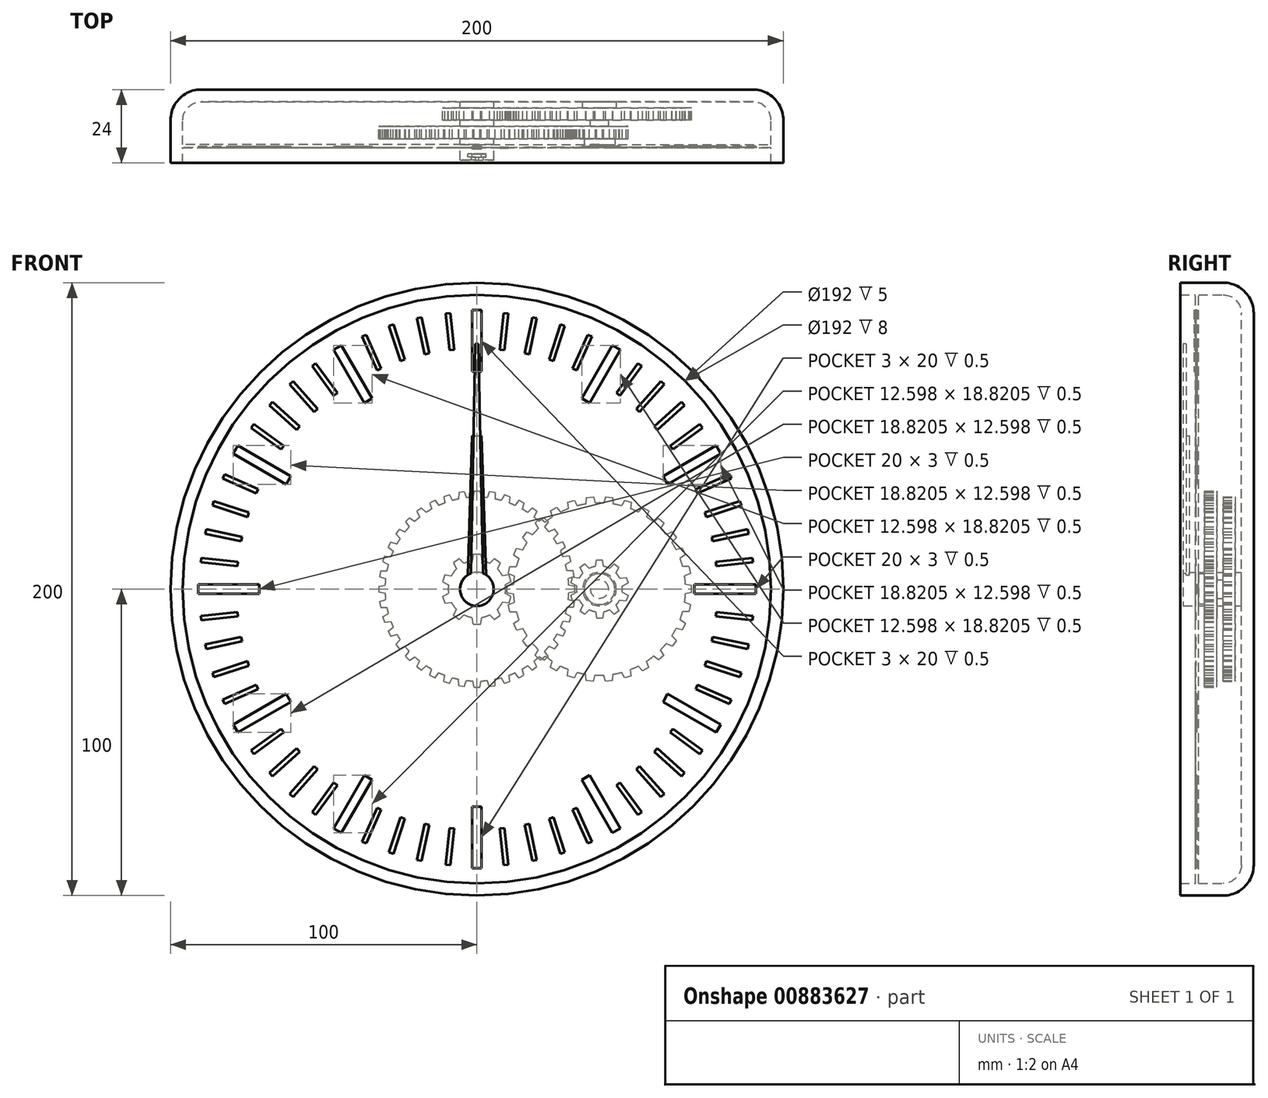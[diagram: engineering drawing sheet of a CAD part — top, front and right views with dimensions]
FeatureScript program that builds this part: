
annotation { "Feature Type Name" : "Feature", "Feature Type Description" : "" }
export const myFeature = defineFeature(function(context is Context, id is Id, definition is map)
    precondition{}
    {
        {
            var Q0;
            Q0=qCreatedBy(makeId("Front.planeOp"),FACE);
            var sketch = newSketch(context, id + "F0", { "sketchPlane" : qUnion([Q0])});
            skCircle(sketch, "E0", {"center": v(0, 0) * mm, "radius": 100 * mm});
            skSolve(sketch);
        }
        {
            var Q0;
            Q0 = qSketchRegion(id + "F0", true);
            extrude(context, id + "F1", {"entities" : qUnion([Q0]), "depth" : 24 * mm, "offsetDistance" : 25 * mm});
        }
        {
            var Q0;
            Q0=makeQuery(id+"F1.opExtrude","CAP_EDGE",EDGE,{"disambiguationData":[OSD([sQuery(id+"F0.wireOp",EDGE,"E0")])],"isStart":true});
            fillet(context, id + "F2", {"entities" : qUnion([Q0]), "radius" : 10 * mm, "tangentPropagation" : true, "allowEdgeOverflow" : false});
        }
        {
            var Q0;
            Q0=makeQuery(id+"F1.opExtrude","CAP_FACE",FACE,{"disambiguationData":[OSD([sQuery(id+"F0.wireOp",EDGE,"E0")])],"isStart":false});
            shell(context, id + "F3", {"entities" : qUnion([Q0]), "thickness" : 4 * mm});
        }
        {
            var Q0;
            {var subQ0=sQuery(id+"F0.wireOp",EDGE,"E0");Q0=makeQuery(id+"F3.opShell","OFFSET_FACE",FACE,{"disambiguationData":[OSD([subQ0]),TDD([makeQuery(id+"F1.opExtrude","CAP_FACE",FACE,{"disambiguationData":[OSD([subQ0])],"isStart":true})])]});}
            var sketch = newSketch(context, id + "F4", { "sketchPlane" : qUnion([Q0])});
            skCircle(sketch, "E1", {"center": v(0, 0) * mm, "radius": 3 * mm});
            skCircle(sketch, "E2", {"center": v(0, 0) * mm, "radius": 5.5 * mm});
            skCircle(sketch, "E3", {"center": v(40, 0) * mm, "radius": 3 * mm});
            skCircle(sketch, "E4", {"center": v(40, 0) * mm, "radius": 5.5 * mm});
            skSolve(sketch);
        }
        {
            var Q0;
            Q0 = qSketchRegion(id + "F4", true);
            extrude(context, id + "F5", {"entities" : qUnion([Q0]), "operationType" : NewBodyOperationType.ADD, "depth" : 2 * mm, "offsetDistance" : 25 * mm});
        }
        {
            var Q0;
            {var subQ0=sQuery(id+"F0.wireOp",EDGE,"E0");Q0=makeQuery(id+"F5.boolean.opBoolean","SPLIT",FACE,{"disambiguationData":[TD([makeQuery(id+"F5.opExtrude","SWEPT_FACE",FACE,{"disambiguationData":[OSD([sQuery(id+"F4.wireOp",EDGE,"E1")])]})])],"derivedFrom":makeQuery(id+"F3.opShell","OFFSET_FACE",FACE,{"disambiguationData":[OSD([subQ0]),TDD([makeQuery(id+"F1.opExtrude","CAP_FACE",FACE,{"disambiguationData":[OSD([subQ0])],"isStart":true})])]})});}
            extrude(context, id + "F6", {"entities" : qUnion([Q0]), "depth" : 19 * mm, "offsetDistance" : 25 * mm});
        }
        {
            var Q0;
            {var subQ0=sQuery(id+"F0.wireOp",EDGE,"E0");Q0=makeQuery(id+"F5.boolean.opBoolean","SPLIT",FACE,{"disambiguationData":[TD([makeQuery(id+"F5.opExtrude","SWEPT_FACE",FACE,{"disambiguationData":[OSD([sQuery(id+"F4.wireOp",EDGE,"E3")])]})])],"derivedFrom":makeQuery(id+"F3.opShell","OFFSET_FACE",FACE,{"disambiguationData":[OSD([subQ0]),TDD([makeQuery(id+"F1.opExtrude","CAP_FACE",FACE,{"disambiguationData":[OSD([subQ0])],"isStart":true})])]})});}
            extrude(context, id + "F7", {"entities" : qUnion([Q0]), "depth" : 8 * mm, "offsetDistance" : 25 * mm});
        }
        {
            var Q0;
            Q0=makeQuery(id+"F5.opExtrude","CAP_FACE",FACE,{"disambiguationData":[OSD([sQuery(id+"F4.wireOp",EDGE,"E1"),sQuery(id+"F4.wireOp",EDGE,"E2")])],"isStart":false});
            var sketch = newSketch(context, id + "F8", { "sketchPlane" : qUnion([Q0])});
            skCircle(sketch, "E5", {"center": v(0, 0) * mm, "radius": 9.38 * mm});
            skLineSegment(sketch, "E6", {"start": v(0, 11.38) * mm, "end": v(1.18, 11.38) * mm});
            skLineSegment(sketch, "E7", {"start": v(1.18, 11.38) * mm, "end": v(1.55, 9.25) * mm});
            skLineSegment(sketch, "E8.MirrorCS", {"start": v(0, 11.38) * mm, "end": v(-1.18, 11.38) * mm});
            skLineSegment(sketch, "E9.MirrorCS", {"start": v(-1.18, 11.38) * mm, "end": v(-1.55, 9.25) * mm});
            skLineSegment(sketch, "E10.1.0", {"start": v(-7.64, 8.51) * mm, "end": v(-6.7, 6.57) * mm});
            skLineSegment(sketch, "E10.1.1", {"start": v(-6.69, 9.2) * mm, "end": v(-7.64, 8.51) * mm});
            skLineSegment(sketch, "E10.1.2", {"start": v(-6.69, 9.2) * mm, "end": v(-5.73, 9.9) * mm});
            skLineSegment(sketch, "E10.1.3", {"start": v(-5.73, 9.9) * mm, "end": v(-4.18, 8.4) * mm});
            skLineSegment(sketch, "E10.2.0", {"start": v(-11.18, 2.4) * mm, "end": v(-9.27, 1.38) * mm});
            skLineSegment(sketch, "E10.2.1", {"start": v(-10.82, 3.52) * mm, "end": v(-11.18, 2.4) * mm});
            skLineSegment(sketch, "E10.2.2", {"start": v(-10.82, 3.52) * mm, "end": v(-10.45, 4.64) * mm});
            skLineSegment(sketch, "E10.2.3", {"start": v(-10.45, 4.64) * mm, "end": v(-8.31, 4.33) * mm});
            skLineSegment(sketch, "E11.2.3.0", {"start": v(-10.45, -4.64) * mm, "end": v(-8.31, -4.33) * mm});
            skLineSegment(sketch, "E11.3.3.0", {"start": v(-10.82, -3.52) * mm, "end": v(-10.45, -4.64) * mm});
            skLineSegment(sketch, "E11.6.3.0", {"start": v(-10.82, -3.52) * mm, "end": v(-11.18, -2.4) * mm});
            skLineSegment(sketch, "E11.9.3.0", {"start": v(-11.18, -2.4) * mm, "end": v(-9.27, -1.38) * mm});
            skLineSegment(sketch, "E11.2.4.0", {"start": v(-5.73, -9.9) * mm, "end": v(-4.18, -8.4) * mm});
            skLineSegment(sketch, "E11.3.4.0", {"start": v(-6.69, -9.2) * mm, "end": v(-5.73, -9.9) * mm});
            skLineSegment(sketch, "E11.6.4.0", {"start": v(-6.69, -9.2) * mm, "end": v(-7.64, -8.51) * mm});
            skLineSegment(sketch, "E11.9.4.0", {"start": v(-7.64, -8.51) * mm, "end": v(-6.7, -6.57) * mm});
            skLineSegment(sketch, "E11.2.5.0", {"start": v(1.18, -11.38) * mm, "end": v(1.55, -9.25) * mm});
            skLineSegment(sketch, "E11.3.5.0", {"start": v(0, -11.38) * mm, "end": v(1.18, -11.38) * mm});
            skLineSegment(sketch, "E11.6.5.0", {"start": v(0, -11.38) * mm, "end": v(-1.18, -11.38) * mm});
            skLineSegment(sketch, "E11.9.5.0", {"start": v(-1.18, -11.38) * mm, "end": v(-1.55, -9.25) * mm});
            skLineSegment(sketch, "E11.2.6.0", {"start": v(7.64, -8.51) * mm, "end": v(6.7, -6.57) * mm});
            skLineSegment(sketch, "E11.3.6.0", {"start": v(6.69, -9.2) * mm, "end": v(7.64, -8.51) * mm});
            skLineSegment(sketch, "E11.6.6.0", {"start": v(6.69, -9.2) * mm, "end": v(5.73, -9.9) * mm});
            skLineSegment(sketch, "E11.9.6.0", {"start": v(5.73, -9.9) * mm, "end": v(4.18, -8.4) * mm});
            skLineSegment(sketch, "E11.2.7.0", {"start": v(11.18, -2.4) * mm, "end": v(9.27, -1.38) * mm});
            skLineSegment(sketch, "E11.3.7.0", {"start": v(10.82, -3.52) * mm, "end": v(11.18, -2.4) * mm});
            skLineSegment(sketch, "E11.6.7.0", {"start": v(10.82, -3.52) * mm, "end": v(10.45, -4.64) * mm});
            skLineSegment(sketch, "E11.9.7.0", {"start": v(10.45, -4.64) * mm, "end": v(8.31, -4.33) * mm});
            skLineSegment(sketch, "E11.2.8.0", {"start": v(10.45, 4.64) * mm, "end": v(8.31, 4.33) * mm});
            skLineSegment(sketch, "E11.3.8.0", {"start": v(10.82, 3.52) * mm, "end": v(10.45, 4.64) * mm});
            skLineSegment(sketch, "E11.6.8.0", {"start": v(10.82, 3.52) * mm, "end": v(11.18, 2.4) * mm});
            skLineSegment(sketch, "E11.9.8.0", {"start": v(11.18, 2.4) * mm, "end": v(9.27, 1.38) * mm});
            skLineSegment(sketch, "E11.2.9.0", {"start": v(5.73, 9.9) * mm, "end": v(4.18, 8.4) * mm});
            skLineSegment(sketch, "E11.3.9.0", {"start": v(6.69, 9.2) * mm, "end": v(5.73, 9.9) * mm});
            skLineSegment(sketch, "E11.6.9.0", {"start": v(6.69, 9.2) * mm, "end": v(7.64, 8.51) * mm});
            skLineSegment(sketch, "E11.9.9.0", {"start": v(7.64, 8.51) * mm, "end": v(6.7, 6.57) * mm});
            skSolve(sketch);
        }
        {
            var Q0;
            Q0 = qSketchRegion(id + "F8", true);
            extrude(context, id + "F9", {"entities" : qUnion([Q0]), "operationType" : NewBodyOperationType.ADD, "depth" : 4 * mm, "offsetDistance" : 25 * mm});
        }
        {
            var Q0;
            Q0=makeQuery(id+"F5.opExtrude","CAP_FACE",FACE,{"disambiguationData":[OSD([sQuery(id+"F4.wireOp",EDGE,"E3"),sQuery(id+"F4.wireOp",EDGE,"E4")])],"isStart":false});
            var sketch = newSketch(context, id + "F10", { "sketchPlane" : qUnion([Q0])});
            skCircle(sketch, "E12", {"center": v(40, 0) * mm, "radius": 28.12 * mm});
            skLineSegment(sketch, "E13", {"start": v(9.88, 0) * mm, "end": v(9.88, 1.18) * mm});
            skLineSegment(sketch, "E14", {"start": v(9.88, 1.18) * mm, "end": v(11.92, 1.54) * mm});
            skLineSegment(sketch, "E15.MirrorCS", {"start": v(9.88, 0) * mm, "end": v(9.88, -1.18) * mm});
            skLineSegment(sketch, "E16.MirrorCS", {"start": v(9.88, -1.18) * mm, "end": v(11.92, -1.54) * mm});
            skLineSegment(sketch, "E17.1.0", {"start": v(10.29, -5.11) * mm, "end": v(12.21, -4.33) * mm});
            skLineSegment(sketch, "E17.1.1", {"start": v(10.53, -6.26) * mm, "end": v(10.29, -5.11) * mm});
            skLineSegment(sketch, "E17.1.2", {"start": v(10.53, -6.26) * mm, "end": v(10.78, -7.42) * mm});
            skLineSegment(sketch, "E17.1.3", {"start": v(10.78, -7.42) * mm, "end": v(12.85, -7.34) * mm});
            skLineSegment(sketch, "E17.2.0", {"start": v(12, -11.18) * mm, "end": v(13.72, -10.02) * mm});
            skLineSegment(sketch, "E17.2.1", {"start": v(12.48, -12.25) * mm, "end": v(12, -11.18) * mm});
            skLineSegment(sketch, "E17.2.2", {"start": v(12.48, -12.25) * mm, "end": v(12.96, -13.33) * mm});
            skLineSegment(sketch, "E17.2.3", {"start": v(12.96, -13.33) * mm, "end": v(14.97, -12.83) * mm});
            skLineSegment(sketch, "E18.1.3.0", {"start": v(14.94, -16.75) * mm, "end": v(16.38, -15.26) * mm});
            skLineSegment(sketch, "E18.3.3.0", {"start": v(15.63, -17.7) * mm, "end": v(14.94, -16.75) * mm});
            skLineSegment(sketch, "E18.6.3.0", {"start": v(15.63, -17.7) * mm, "end": v(16.32, -18.66) * mm});
            skLineSegment(sketch, "E18.9.3.0", {"start": v(16.32, -18.66) * mm, "end": v(18.18, -17.75) * mm});
            skLineSegment(sketch, "E18.1.4.0", {"start": v(18.97, -21.6) * mm, "end": v(20.07, -19.84) * mm});
            skLineSegment(sketch, "E18.3.4.0", {"start": v(19.84, -22.39) * mm, "end": v(18.97, -21.6) * mm});
            skLineSegment(sketch, "E18.6.4.0", {"start": v(19.84, -22.39) * mm, "end": v(20.72, -23.18) * mm});
            skLineSegment(sketch, "E18.9.4.0", {"start": v(20.72, -23.18) * mm, "end": v(22.35, -21.9) * mm});
            skLineSegment(sketch, "E18.1.5.0", {"start": v(23.92, -25.5) * mm, "end": v(24.63, -23.55) * mm});
            skLineSegment(sketch, "E18.3.5.0", {"start": v(24.94, -26.09) * mm, "end": v(23.92, -25.5) * mm});
            skLineSegment(sketch, "E18.6.5.0", {"start": v(24.94, -26.09) * mm, "end": v(25.96, -26.68) * mm});
            skLineSegment(sketch, "E18.9.5.0", {"start": v(25.96, -26.68) * mm, "end": v(27.3, -25.09) * mm});
            skLineSegment(sketch, "E18.1.6.0", {"start": v(29.57, -28.29) * mm, "end": v(29.86, -26.23) * mm});
            skLineSegment(sketch, "E18.3.6.0", {"start": v(30.7, -28.65) * mm, "end": v(29.57, -28.29) * mm});
            skLineSegment(sketch, "E18.6.6.0", {"start": v(30.7, -28.65) * mm, "end": v(31.81, -29.01) * mm});
            skLineSegment(sketch, "E18.9.6.0", {"start": v(31.81, -29.01) * mm, "end": v(32.78, -27.18) * mm});
            skLineSegment(sketch, "E18.1.7.0", {"start": v(35.68, -29.84) * mm, "end": v(35.53, -27.77) * mm});
            skLineSegment(sketch, "E18.3.7.0", {"start": v(36.85, -29.96) * mm, "end": v(35.68, -29.84) * mm});
            skLineSegment(sketch, "E18.6.7.0", {"start": v(36.85, -29.96) * mm, "end": v(38.02, -30.08) * mm});
            skLineSegment(sketch, "E18.9.7.0", {"start": v(38.02, -30.08) * mm, "end": v(38.6, -28.09) * mm});
            skLineSegment(sketch, "E18.1.8.0", {"start": v(41.98, -30.08) * mm, "end": v(41.4, -28.09) * mm});
            skLineSegment(sketch, "E18.3.8.0", {"start": v(43.15, -29.96) * mm, "end": v(41.98, -30.08) * mm});
            skLineSegment(sketch, "E18.6.8.0", {"start": v(43.15, -29.96) * mm, "end": v(44.32, -29.84) * mm});
            skLineSegment(sketch, "E18.9.8.0", {"start": v(44.32, -29.84) * mm, "end": v(44.47, -27.77) * mm});
            skLineSegment(sketch, "E18.1.9.0", {"start": v(48.19, -29.01) * mm, "end": v(47.22, -27.18) * mm});
            skLineSegment(sketch, "E18.3.9.0", {"start": v(49.3, -28.65) * mm, "end": v(48.19, -29.01) * mm});
            skLineSegment(sketch, "E18.6.9.0", {"start": v(49.3, -28.65) * mm, "end": v(50.43, -28.29) * mm});
            skLineSegment(sketch, "E18.9.9.0", {"start": v(50.43, -28.29) * mm, "end": v(50.14, -26.23) * mm});
            skLineSegment(sketch, "E18.1.10.0", {"start": v(54.04, -26.68) * mm, "end": v(52.7, -25.09) * mm});
            skLineSegment(sketch, "E18.3.10.0", {"start": v(55.06, -26.09) * mm, "end": v(54.04, -26.68) * mm});
            skLineSegment(sketch, "E18.6.10.0", {"start": v(55.06, -26.09) * mm, "end": v(56.08, -25.5) * mm});
            skLineSegment(sketch, "E18.9.10.0", {"start": v(56.08, -25.5) * mm, "end": v(55.37, -23.55) * mm});
            skLineSegment(sketch, "E18.1.11.0", {"start": v(59.28, -23.18) * mm, "end": v(57.65, -21.9) * mm});
            skLineSegment(sketch, "E18.3.11.0", {"start": v(60.16, -22.39) * mm, "end": v(59.28, -23.18) * mm});
            skLineSegment(sketch, "E18.6.11.0", {"start": v(60.16, -22.39) * mm, "end": v(61.03, -21.6) * mm});
            skLineSegment(sketch, "E18.9.11.0", {"start": v(61.03, -21.6) * mm, "end": v(59.93, -19.84) * mm});
            skLineSegment(sketch, "E18.1.12.0", {"start": v(63.68, -18.66) * mm, "end": v(61.82, -17.75) * mm});
            skLineSegment(sketch, "E18.3.12.0", {"start": v(64.37, -17.7) * mm, "end": v(63.68, -18.66) * mm});
            skLineSegment(sketch, "E18.6.12.0", {"start": v(64.37, -17.7) * mm, "end": v(65.06, -16.75) * mm});
            skLineSegment(sketch, "E18.9.12.0", {"start": v(65.06, -16.75) * mm, "end": v(63.62, -15.26) * mm});
            skLineSegment(sketch, "E18.1.13.0", {"start": v(67.04, -13.33) * mm, "end": v(65.03, -12.83) * mm});
            skLineSegment(sketch, "E18.3.13.0", {"start": v(67.52, -12.25) * mm, "end": v(67.04, -13.33) * mm});
            skLineSegment(sketch, "E18.6.13.0", {"start": v(67.52, -12.25) * mm, "end": v(68, -11.18) * mm});
            skLineSegment(sketch, "E18.9.13.0", {"start": v(68, -11.18) * mm, "end": v(66.28, -10.02) * mm});
            skLineSegment(sketch, "E18.1.14.0", {"start": v(69.22, -7.42) * mm, "end": v(67.15, -7.34) * mm});
            skLineSegment(sketch, "E18.3.14.0", {"start": v(69.47, -6.26) * mm, "end": v(69.22, -7.42) * mm});
            skLineSegment(sketch, "E18.6.14.0", {"start": v(69.47, -6.26) * mm, "end": v(69.71, -5.11) * mm});
            skLineSegment(sketch, "E18.9.14.0", {"start": v(69.71, -5.11) * mm, "end": v(67.79, -4.33) * mm});
            skLineSegment(sketch, "E18.1.15.0", {"start": v(70.13, -1.18) * mm, "end": v(68.08, -1.54) * mm});
            skLineSegment(sketch, "E18.3.15.0", {"start": v(70.12, 0) * mm, "end": v(70.12, -1.18) * mm});
            skLineSegment(sketch, "E18.6.15.0", {"start": v(70.12, 0) * mm, "end": v(70.12, 1.18) * mm});
            skLineSegment(sketch, "E18.9.15.0", {"start": v(70.13, 1.18) * mm, "end": v(68.08, 1.54) * mm});
            skLineSegment(sketch, "E18.1.16.0", {"start": v(69.71, 5.11) * mm, "end": v(67.79, 4.33) * mm});
            skLineSegment(sketch, "E18.3.16.0", {"start": v(69.47, 6.26) * mm, "end": v(69.71, 5.11) * mm});
            skLineSegment(sketch, "E18.6.16.0", {"start": v(69.47, 6.26) * mm, "end": v(69.22, 7.42) * mm});
            skLineSegment(sketch, "E18.9.16.0", {"start": v(69.22, 7.42) * mm, "end": v(67.15, 7.34) * mm});
            skLineSegment(sketch, "E18.1.17.0", {"start": v(68, 11.18) * mm, "end": v(66.28, 10.02) * mm});
            skLineSegment(sketch, "E18.3.17.0", {"start": v(67.52, 12.25) * mm, "end": v(68, 11.18) * mm});
            skLineSegment(sketch, "E18.6.17.0", {"start": v(67.52, 12.25) * mm, "end": v(67.04, 13.33) * mm});
            skLineSegment(sketch, "E18.9.17.0", {"start": v(67.04, 13.33) * mm, "end": v(65.03, 12.83) * mm});
            skLineSegment(sketch, "E18.1.18.0", {"start": v(65.06, 16.75) * mm, "end": v(63.62, 15.26) * mm});
            skLineSegment(sketch, "E18.3.18.0", {"start": v(64.37, 17.7) * mm, "end": v(65.06, 16.75) * mm});
            skLineSegment(sketch, "E18.6.18.0", {"start": v(64.37, 17.7) * mm, "end": v(63.68, 18.66) * mm});
            skLineSegment(sketch, "E18.9.18.0", {"start": v(63.68, 18.66) * mm, "end": v(61.82, 17.75) * mm});
            skLineSegment(sketch, "E18.1.19.0", {"start": v(61.03, 21.6) * mm, "end": v(59.93, 19.84) * mm});
            skLineSegment(sketch, "E18.3.19.0", {"start": v(60.16, 22.39) * mm, "end": v(61.03, 21.6) * mm});
            skLineSegment(sketch, "E18.6.19.0", {"start": v(60.16, 22.39) * mm, "end": v(59.28, 23.18) * mm});
            skLineSegment(sketch, "E18.9.19.0", {"start": v(59.28, 23.18) * mm, "end": v(57.65, 21.9) * mm});
            skLineSegment(sketch, "E18.1.20.0", {"start": v(56.08, 25.5) * mm, "end": v(55.37, 23.55) * mm});
            skLineSegment(sketch, "E18.3.20.0", {"start": v(55.06, 26.09) * mm, "end": v(56.08, 25.5) * mm});
            skLineSegment(sketch, "E18.6.20.0", {"start": v(55.06, 26.09) * mm, "end": v(54.04, 26.68) * mm});
            skLineSegment(sketch, "E18.9.20.0", {"start": v(54.04, 26.68) * mm, "end": v(52.7, 25.09) * mm});
            skLineSegment(sketch, "E18.1.21.0", {"start": v(50.43, 28.29) * mm, "end": v(50.14, 26.23) * mm});
            skLineSegment(sketch, "E18.3.21.0", {"start": v(49.3, 28.65) * mm, "end": v(50.43, 28.29) * mm});
            skLineSegment(sketch, "E18.6.21.0", {"start": v(49.3, 28.65) * mm, "end": v(48.19, 29.01) * mm});
            skLineSegment(sketch, "E18.9.21.0", {"start": v(48.19, 29.01) * mm, "end": v(47.22, 27.18) * mm});
            skLineSegment(sketch, "E18.1.22.0", {"start": v(44.32, 29.84) * mm, "end": v(44.47, 27.77) * mm});
            skLineSegment(sketch, "E18.3.22.0", {"start": v(43.15, 29.96) * mm, "end": v(44.32, 29.84) * mm});
            skLineSegment(sketch, "E18.6.22.0", {"start": v(43.15, 29.96) * mm, "end": v(41.98, 30.08) * mm});
            skLineSegment(sketch, "E18.9.22.0", {"start": v(41.98, 30.08) * mm, "end": v(41.4, 28.09) * mm});
            skLineSegment(sketch, "E18.1.23.0", {"start": v(38.02, 30.08) * mm, "end": v(38.6, 28.09) * mm});
            skLineSegment(sketch, "E18.3.23.0", {"start": v(36.85, 29.96) * mm, "end": v(38.02, 30.08) * mm});
            skLineSegment(sketch, "E18.6.23.0", {"start": v(36.85, 29.96) * mm, "end": v(35.68, 29.84) * mm});
            skLineSegment(sketch, "E18.9.23.0", {"start": v(35.68, 29.84) * mm, "end": v(35.53, 27.77) * mm});
            skLineSegment(sketch, "E18.1.24.0", {"start": v(31.81, 29.01) * mm, "end": v(32.78, 27.18) * mm});
            skLineSegment(sketch, "E18.3.24.0", {"start": v(30.7, 28.65) * mm, "end": v(31.81, 29.01) * mm});
            skLineSegment(sketch, "E18.6.24.0", {"start": v(30.7, 28.65) * mm, "end": v(29.57, 28.29) * mm});
            skLineSegment(sketch, "E18.9.24.0", {"start": v(29.57, 28.29) * mm, "end": v(29.86, 26.23) * mm});
            skLineSegment(sketch, "E18.1.25.0", {"start": v(25.96, 26.68) * mm, "end": v(27.3, 25.09) * mm});
            skLineSegment(sketch, "E18.3.25.0", {"start": v(24.94, 26.09) * mm, "end": v(25.96, 26.68) * mm});
            skLineSegment(sketch, "E18.6.25.0", {"start": v(24.94, 26.09) * mm, "end": v(23.92, 25.5) * mm});
            skLineSegment(sketch, "E18.9.25.0", {"start": v(23.92, 25.5) * mm, "end": v(24.63, 23.55) * mm});
            skLineSegment(sketch, "E18.1.26.0", {"start": v(20.72, 23.18) * mm, "end": v(22.35, 21.9) * mm});
            skLineSegment(sketch, "E18.3.26.0", {"start": v(19.84, 22.39) * mm, "end": v(20.72, 23.18) * mm});
            skLineSegment(sketch, "E18.6.26.0", {"start": v(19.84, 22.39) * mm, "end": v(18.97, 21.6) * mm});
            skLineSegment(sketch, "E18.9.26.0", {"start": v(18.97, 21.6) * mm, "end": v(20.07, 19.84) * mm});
            skLineSegment(sketch, "E18.1.27.0", {"start": v(16.32, 18.66) * mm, "end": v(18.18, 17.75) * mm});
            skLineSegment(sketch, "E18.3.27.0", {"start": v(15.63, 17.7) * mm, "end": v(16.32, 18.66) * mm});
            skLineSegment(sketch, "E18.6.27.0", {"start": v(15.63, 17.7) * mm, "end": v(14.94, 16.75) * mm});
            skLineSegment(sketch, "E18.9.27.0", {"start": v(14.94, 16.75) * mm, "end": v(16.38, 15.26) * mm});
            skLineSegment(sketch, "E18.1.28.0", {"start": v(12.96, 13.33) * mm, "end": v(14.97, 12.83) * mm});
            skLineSegment(sketch, "E18.3.28.0", {"start": v(12.48, 12.25) * mm, "end": v(12.96, 13.33) * mm});
            skLineSegment(sketch, "E18.6.28.0", {"start": v(12.48, 12.25) * mm, "end": v(12, 11.18) * mm});
            skLineSegment(sketch, "E18.9.28.0", {"start": v(12, 11.18) * mm, "end": v(13.72, 10.02) * mm});
            skLineSegment(sketch, "E18.1.29.0", {"start": v(10.78, 7.42) * mm, "end": v(12.85, 7.34) * mm});
            skLineSegment(sketch, "E18.3.29.0", {"start": v(10.53, 6.26) * mm, "end": v(10.78, 7.42) * mm});
            skLineSegment(sketch, "E18.6.29.0", {"start": v(10.53, 6.26) * mm, "end": v(10.29, 5.11) * mm});
            skLineSegment(sketch, "E18.9.29.0", {"start": v(10.29, 5.11) * mm, "end": v(12.21, 4.33) * mm});
            skSolve(sketch);
        }
        {
            var Q0;
            Q0 = qSketchRegion(id + "F10", true);
            extrude(context, id + "F11", {"entities" : qUnion([Q0]), "operationType" : NewBodyOperationType.ADD, "depth" : 4 * mm, "offsetDistance" : 25 * mm});
        }
        {
            var Q0;
            Q0=makeQuery(id+"F9.opExtrude","CAP_FACE",FACE,{"disambiguationData":[OSD([sQuery(id+"F8.wireOp",EDGE,"E5"),sQuery(id+"F8.wireOp",EDGE,"E6"),sQuery(id+"F8.wireOp",EDGE,"E7"),sQuery(id+"F8.wireOp",EDGE,"E8.MirrorCS"),sQuery(id+"F8.wireOp",EDGE,"E9.MirrorCS"),sQuery(id+"F8.wireOp",EDGE,"E10.1.0"),sQuery(id+"F8.wireOp",EDGE,"E10.1.1"),sQuery(id+"F8.wireOp",EDGE,"E10.1.2"),sQuery(id+"F8.wireOp",EDGE,"E10.1.3"),sQuery(id+"F8.wireOp",EDGE,"E10.2.0"),sQuery(id+"F8.wireOp",EDGE,"E10.2.1"),sQuery(id+"F8.wireOp",EDGE,"E10.2.2"),sQuery(id+"F8.wireOp",EDGE,"E10.2.3"),sQuery(id+"F8.wireOp",EDGE,"E11.2.3.0"),sQuery(id+"F8.wireOp",EDGE,"E11.3.3.0"),sQuery(id+"F8.wireOp",EDGE,"E11.6.3.0"),sQuery(id+"F8.wireOp",EDGE,"E11.9.3.0"),sQuery(id+"F8.wireOp",EDGE,"E11.2.4.0"),sQuery(id+"F8.wireOp",EDGE,"E11.3.4.0"),sQuery(id+"F8.wireOp",EDGE,"E11.6.4.0"),sQuery(id+"F8.wireOp",EDGE,"E11.9.4.0"),sQuery(id+"F8.wireOp",EDGE,"E11.2.5.0"),sQuery(id+"F8.wireOp",EDGE,"E11.3.5.0"),sQuery(id+"F8.wireOp",EDGE,"E11.6.5.0"),sQuery(id+"F8.wireOp",EDGE,"E11.9.5.0"),sQuery(id+"F8.wireOp",EDGE,"E11.2.6.0"),sQuery(id+"F8.wireOp",EDGE,"E11.3.6.0"),sQuery(id+"F8.wireOp",EDGE,"E11.6.6.0"),sQuery(id+"F8.wireOp",EDGE,"E11.9.6.0"),sQuery(id+"F8.wireOp",EDGE,"E11.2.7.0"),sQuery(id+"F8.wireOp",EDGE,"E11.3.7.0"),sQuery(id+"F8.wireOp",EDGE,"E11.6.7.0"),sQuery(id+"F8.wireOp",EDGE,"E11.9.7.0"),sQuery(id+"F8.wireOp",EDGE,"E11.2.8.0"),sQuery(id+"F8.wireOp",EDGE,"E11.3.8.0"),sQuery(id+"F8.wireOp",EDGE,"E11.6.8.0"),sQuery(id+"F8.wireOp",EDGE,"E11.9.8.0"),sQuery(id+"F8.wireOp",EDGE,"E11.2.9.0"),sQuery(id+"F8.wireOp",EDGE,"E11.3.9.0"),sQuery(id+"F8.wireOp",EDGE,"E11.6.9.0"),sQuery(id+"F8.wireOp",EDGE,"E11.9.9.0")])],"isStart":false});
            var sketch = newSketch(context, id + "F12", { "sketchPlane" : qUnion([Q0])});
            skCircle(sketch, "E19.0", {"center": v(0, 0) * mm, "radius": 3 * mm});
            skCircle(sketch, "E20.0", {"center": v(0, 0) * mm, "radius": 5.5 * mm});
            skSolve(sketch);
        }
        {
            var Q0;
            Q0 = qSketchRegion(id + "F12", true);
            extrude(context, id + "F13", {"entities" : qUnion([Q0]), "depth" : 2 * mm, "offsetDistance" : 25 * mm});
        }
        {
            var Q0;
            Q0=makeQuery(id+"F13.opExtrude","CAP_FACE",FACE,{"disambiguationData":[OSD([sQuery(id+"F12.wireOp",EDGE,"E19.0"),sQuery(id+"F12.wireOp",EDGE,"E20.0")])],"isStart":false});
            var sketch = newSketch(context, id + "F14", { "sketchPlane" : qUnion([Q0])});
            skCircle(sketch, "E21.0", {"center": v(0, 0) * mm, "radius": 3 * mm});
            skCircle(sketch, "E22", {"center": v(0, 0) * mm, "radius": 30 * mm});
            skLineSegment(sketch, "E23", {"start": v(0, 32) * mm, "end": v(0.94, 32) * mm});
            skLineSegment(sketch, "E24", {"start": v(0.94, 32) * mm, "end": v(1.3, 29.97) * mm});
            skLineSegment(sketch, "E25.MirrorCS", {"start": v(0, 32) * mm, "end": v(-0.94, 32) * mm});
            skLineSegment(sketch, "E26.MirrorCS", {"start": v(-0.94, 32) * mm, "end": v(-1.3, 29.97) * mm});
            skLineSegment(sketch, "E27.1.0", {"start": v(-5.94, 31.46) * mm, "end": v(-5.97, 29.4) * mm});
            skLineSegment(sketch, "E27.1.1", {"start": v(-5, 31.6) * mm, "end": v(-5.94, 31.46) * mm});
            skLineSegment(sketch, "E27.1.2", {"start": v(-5, 31.6) * mm, "end": v(-4.08, 31.75) * mm});
            skLineSegment(sketch, "E27.1.3", {"start": v(-4.08, 31.75) * mm, "end": v(-3.4, 29.8) * mm});
            skLineSegment(sketch, "E27.2.0", {"start": v(-10.78, 30.14) * mm, "end": v(-10.5, 28.1) * mm});
            skLineSegment(sketch, "E27.2.1", {"start": v(-9.89, 30.43) * mm, "end": v(-10.78, 30.14) * mm});
            skLineSegment(sketch, "E27.2.2", {"start": v(-9.89, 30.43) * mm, "end": v(-9, 30.73) * mm});
            skLineSegment(sketch, "E27.2.3", {"start": v(-9, 30.73) * mm, "end": v(-8.03, 28.9) * mm});
            skLineSegment(sketch, "E28.2.3.0", {"start": v(-15.37, 28.08) * mm, "end": v(-14.77, 26.11) * mm});
            skLineSegment(sketch, "E28.3.3.0", {"start": v(-14.53, 28.51) * mm, "end": v(-15.37, 28.08) * mm});
            skLineSegment(sketch, "E28.6.3.0", {"start": v(-14.53, 28.51) * mm, "end": v(-13.69, 28.94) * mm});
            skLineSegment(sketch, "E28.9.3.0", {"start": v(-13.69, 28.94) * mm, "end": v(-12.45, 27.3) * mm});
            skLineSegment(sketch, "E28.2.4.0", {"start": v(-19.57, 25.33) * mm, "end": v(-18.67, 23.48) * mm});
            skLineSegment(sketch, "E28.3.4.0", {"start": v(-18.8, 25.89) * mm, "end": v(-19.57, 25.33) * mm});
            skLineSegment(sketch, "E28.6.4.0", {"start": v(-18.8, 25.89) * mm, "end": v(-18.05, 26.44) * mm});
            skLineSegment(sketch, "E28.9.4.0", {"start": v(-18.05, 26.44) * mm, "end": v(-16.57, 25.01) * mm});
            skLineSegment(sketch, "E28.2.5.0", {"start": v(-23.3, 21.96) * mm, "end": v(-22.11, 20.27) * mm});
            skLineSegment(sketch, "E28.3.5.0", {"start": v(-22.63, 22.63) * mm, "end": v(-23.3, 21.96) * mm});
            skLineSegment(sketch, "E28.6.5.0", {"start": v(-22.63, 22.63) * mm, "end": v(-21.96, 23.3) * mm});
            skLineSegment(sketch, "E28.9.5.0", {"start": v(-21.96, 23.3) * mm, "end": v(-20.27, 22.11) * mm});
            skLineSegment(sketch, "E28.2.6.0", {"start": v(-26.44, 18.05) * mm, "end": v(-25.01, 16.57) * mm});
            skLineSegment(sketch, "E28.3.6.0", {"start": v(-25.89, 18.8) * mm, "end": v(-26.44, 18.05) * mm});
            skLineSegment(sketch, "E28.6.6.0", {"start": v(-25.89, 18.8) * mm, "end": v(-25.33, 19.57) * mm});
            skLineSegment(sketch, "E28.9.6.0", {"start": v(-25.33, 19.57) * mm, "end": v(-23.48, 18.67) * mm});
            skLineSegment(sketch, "E28.2.7.0", {"start": v(-28.94, 13.69) * mm, "end": v(-27.3, 12.45) * mm});
            skLineSegment(sketch, "E28.3.7.0", {"start": v(-28.51, 14.53) * mm, "end": v(-28.94, 13.69) * mm});
            skLineSegment(sketch, "E28.6.7.0", {"start": v(-28.51, 14.53) * mm, "end": v(-28.08, 15.37) * mm});
            skLineSegment(sketch, "E28.9.7.0", {"start": v(-28.08, 15.37) * mm, "end": v(-26.11, 14.77) * mm});
            skLineSegment(sketch, "E28.2.8.0", {"start": v(-30.73, 9) * mm, "end": v(-28.9, 8.03) * mm});
            skLineSegment(sketch, "E28.3.8.0", {"start": v(-30.43, 9.89) * mm, "end": v(-30.73, 9) * mm});
            skLineSegment(sketch, "E28.6.8.0", {"start": v(-30.43, 9.89) * mm, "end": v(-30.14, 10.78) * mm});
            skLineSegment(sketch, "E28.9.8.0", {"start": v(-30.14, 10.78) * mm, "end": v(-28.1, 10.5) * mm});
            skLineSegment(sketch, "E28.2.9.0", {"start": v(-31.75, 4.08) * mm, "end": v(-29.8, 3.4) * mm});
            skLineSegment(sketch, "E28.3.9.0", {"start": v(-31.6, 5) * mm, "end": v(-31.75, 4.08) * mm});
            skLineSegment(sketch, "E28.6.9.0", {"start": v(-31.6, 5) * mm, "end": v(-31.46, 5.94) * mm});
            skLineSegment(sketch, "E28.9.9.0", {"start": v(-31.46, 5.94) * mm, "end": v(-29.4, 5.97) * mm});
            skLineSegment(sketch, "E28.2.10.0", {"start": v(-32, -0.94) * mm, "end": v(-29.97, -1.3) * mm});
            skLineSegment(sketch, "E28.3.10.0", {"start": v(-32, 0) * mm, "end": v(-32, -0.94) * mm});
            skLineSegment(sketch, "E28.6.10.0", {"start": v(-32, 0) * mm, "end": v(-32, 0.94) * mm});
            skLineSegment(sketch, "E28.9.10.0", {"start": v(-32, 0.94) * mm, "end": v(-29.97, 1.3) * mm});
            skLineSegment(sketch, "E28.2.11.0", {"start": v(-31.46, -5.94) * mm, "end": v(-29.4, -5.97) * mm});
            skLineSegment(sketch, "E28.3.11.0", {"start": v(-31.6, -5) * mm, "end": v(-31.46, -5.94) * mm});
            skLineSegment(sketch, "E28.6.11.0", {"start": v(-31.6, -5) * mm, "end": v(-31.75, -4.08) * mm});
            skLineSegment(sketch, "E28.9.11.0", {"start": v(-31.75, -4.08) * mm, "end": v(-29.8, -3.4) * mm});
            skLineSegment(sketch, "E28.2.12.0", {"start": v(-30.14, -10.78) * mm, "end": v(-28.1, -10.5) * mm});
            skLineSegment(sketch, "E28.3.12.0", {"start": v(-30.43, -9.89) * mm, "end": v(-30.14, -10.78) * mm});
            skLineSegment(sketch, "E28.6.12.0", {"start": v(-30.43, -9.89) * mm, "end": v(-30.73, -9) * mm});
            skLineSegment(sketch, "E28.9.12.0", {"start": v(-30.73, -9) * mm, "end": v(-28.9, -8.03) * mm});
            skLineSegment(sketch, "E28.2.13.0", {"start": v(-28.08, -15.37) * mm, "end": v(-26.11, -14.77) * mm});
            skLineSegment(sketch, "E28.3.13.0", {"start": v(-28.51, -14.53) * mm, "end": v(-28.08, -15.37) * mm});
            skLineSegment(sketch, "E28.6.13.0", {"start": v(-28.51, -14.53) * mm, "end": v(-28.94, -13.69) * mm});
            skLineSegment(sketch, "E28.9.13.0", {"start": v(-28.94, -13.69) * mm, "end": v(-27.3, -12.45) * mm});
            skLineSegment(sketch, "E28.2.14.0", {"start": v(-25.33, -19.57) * mm, "end": v(-23.48, -18.67) * mm});
            skLineSegment(sketch, "E28.3.14.0", {"start": v(-25.89, -18.8) * mm, "end": v(-25.33, -19.57) * mm});
            skLineSegment(sketch, "E28.6.14.0", {"start": v(-25.89, -18.8) * mm, "end": v(-26.44, -18.05) * mm});
            skLineSegment(sketch, "E28.9.14.0", {"start": v(-26.44, -18.05) * mm, "end": v(-25.01, -16.57) * mm});
            skLineSegment(sketch, "E28.2.15.0", {"start": v(-21.96, -23.3) * mm, "end": v(-20.27, -22.11) * mm});
            skLineSegment(sketch, "E28.3.15.0", {"start": v(-22.63, -22.63) * mm, "end": v(-21.96, -23.3) * mm});
            skLineSegment(sketch, "E28.6.15.0", {"start": v(-22.63, -22.63) * mm, "end": v(-23.3, -21.96) * mm});
            skLineSegment(sketch, "E28.9.15.0", {"start": v(-23.3, -21.96) * mm, "end": v(-22.11, -20.27) * mm});
            skLineSegment(sketch, "E28.2.16.0", {"start": v(-18.05, -26.44) * mm, "end": v(-16.57, -25.01) * mm});
            skLineSegment(sketch, "E28.3.16.0", {"start": v(-18.8, -25.89) * mm, "end": v(-18.05, -26.44) * mm});
            skLineSegment(sketch, "E28.6.16.0", {"start": v(-18.8, -25.89) * mm, "end": v(-19.57, -25.33) * mm});
            skLineSegment(sketch, "E28.9.16.0", {"start": v(-19.57, -25.33) * mm, "end": v(-18.67, -23.48) * mm});
            skLineSegment(sketch, "E28.2.17.0", {"start": v(-13.69, -28.94) * mm, "end": v(-12.45, -27.3) * mm});
            skLineSegment(sketch, "E28.3.17.0", {"start": v(-14.53, -28.51) * mm, "end": v(-13.69, -28.94) * mm});
            skLineSegment(sketch, "E28.6.17.0", {"start": v(-14.53, -28.51) * mm, "end": v(-15.37, -28.08) * mm});
            skLineSegment(sketch, "E28.9.17.0", {"start": v(-15.37, -28.08) * mm, "end": v(-14.77, -26.11) * mm});
            skLineSegment(sketch, "E28.2.18.0", {"start": v(-9, -30.73) * mm, "end": v(-8.03, -28.9) * mm});
            skLineSegment(sketch, "E28.3.18.0", {"start": v(-9.89, -30.43) * mm, "end": v(-9, -30.73) * mm});
            skLineSegment(sketch, "E28.6.18.0", {"start": v(-9.89, -30.43) * mm, "end": v(-10.78, -30.14) * mm});
            skLineSegment(sketch, "E28.9.18.0", {"start": v(-10.78, -30.14) * mm, "end": v(-10.5, -28.1) * mm});
            skLineSegment(sketch, "E28.2.19.0", {"start": v(-4.08, -31.75) * mm, "end": v(-3.4, -29.8) * mm});
            skLineSegment(sketch, "E28.3.19.0", {"start": v(-5, -31.6) * mm, "end": v(-4.08, -31.75) * mm});
            skLineSegment(sketch, "E28.6.19.0", {"start": v(-5, -31.6) * mm, "end": v(-5.94, -31.46) * mm});
            skLineSegment(sketch, "E28.9.19.0", {"start": v(-5.94, -31.46) * mm, "end": v(-5.97, -29.4) * mm});
            skLineSegment(sketch, "E28.2.20.0", {"start": v(0.94, -32) * mm, "end": v(1.3, -29.97) * mm});
            skLineSegment(sketch, "E28.3.20.0", {"start": v(0, -32) * mm, "end": v(0.94, -32) * mm});
            skLineSegment(sketch, "E28.6.20.0", {"start": v(0, -32) * mm, "end": v(-0.94, -32) * mm});
            skLineSegment(sketch, "E28.9.20.0", {"start": v(-0.94, -32) * mm, "end": v(-1.3, -29.97) * mm});
            skLineSegment(sketch, "E28.2.21.0", {"start": v(5.94, -31.46) * mm, "end": v(5.97, -29.4) * mm});
            skLineSegment(sketch, "E28.3.21.0", {"start": v(5, -31.6) * mm, "end": v(5.94, -31.46) * mm});
            skLineSegment(sketch, "E28.6.21.0", {"start": v(5, -31.6) * mm, "end": v(4.08, -31.75) * mm});
            skLineSegment(sketch, "E28.9.21.0", {"start": v(4.08, -31.75) * mm, "end": v(3.4, -29.8) * mm});
            skLineSegment(sketch, "E28.2.22.0", {"start": v(10.78, -30.14) * mm, "end": v(10.5, -28.1) * mm});
            skLineSegment(sketch, "E28.3.22.0", {"start": v(9.89, -30.43) * mm, "end": v(10.78, -30.14) * mm});
            skLineSegment(sketch, "E28.6.22.0", {"start": v(9.89, -30.43) * mm, "end": v(9, -30.73) * mm});
            skLineSegment(sketch, "E28.9.22.0", {"start": v(9, -30.73) * mm, "end": v(8.03, -28.9) * mm});
            skLineSegment(sketch, "E28.2.23.0", {"start": v(15.37, -28.08) * mm, "end": v(14.77, -26.11) * mm});
            skLineSegment(sketch, "E28.3.23.0", {"start": v(14.53, -28.51) * mm, "end": v(15.37, -28.08) * mm});
            skLineSegment(sketch, "E28.6.23.0", {"start": v(14.53, -28.51) * mm, "end": v(13.69, -28.94) * mm});
            skLineSegment(sketch, "E28.9.23.0", {"start": v(13.69, -28.94) * mm, "end": v(12.45, -27.3) * mm});
            skLineSegment(sketch, "E28.2.24.0", {"start": v(19.57, -25.33) * mm, "end": v(18.67, -23.48) * mm});
            skLineSegment(sketch, "E28.3.24.0", {"start": v(18.8, -25.89) * mm, "end": v(19.57, -25.33) * mm});
            skLineSegment(sketch, "E28.6.24.0", {"start": v(18.8, -25.89) * mm, "end": v(18.05, -26.44) * mm});
            skLineSegment(sketch, "E28.9.24.0", {"start": v(18.05, -26.44) * mm, "end": v(16.57, -25.01) * mm});
            skLineSegment(sketch, "E28.2.25.0", {"start": v(23.3, -21.96) * mm, "end": v(22.11, -20.27) * mm});
            skLineSegment(sketch, "E28.3.25.0", {"start": v(22.63, -22.63) * mm, "end": v(23.3, -21.96) * mm});
            skLineSegment(sketch, "E28.6.25.0", {"start": v(22.63, -22.63) * mm, "end": v(21.96, -23.3) * mm});
            skLineSegment(sketch, "E28.9.25.0", {"start": v(21.96, -23.3) * mm, "end": v(20.27, -22.11) * mm});
            skLineSegment(sketch, "E28.2.26.0", {"start": v(26.44, -18.05) * mm, "end": v(25.01, -16.57) * mm});
            skLineSegment(sketch, "E28.3.26.0", {"start": v(25.89, -18.8) * mm, "end": v(26.44, -18.05) * mm});
            skLineSegment(sketch, "E28.6.26.0", {"start": v(25.89, -18.8) * mm, "end": v(25.33, -19.57) * mm});
            skLineSegment(sketch, "E28.9.26.0", {"start": v(25.33, -19.57) * mm, "end": v(23.48, -18.67) * mm});
            skLineSegment(sketch, "E28.2.27.0", {"start": v(28.94, -13.69) * mm, "end": v(27.3, -12.45) * mm});
            skLineSegment(sketch, "E28.3.27.0", {"start": v(28.51, -14.53) * mm, "end": v(28.94, -13.69) * mm});
            skLineSegment(sketch, "E28.6.27.0", {"start": v(28.51, -14.53) * mm, "end": v(28.08, -15.37) * mm});
            skLineSegment(sketch, "E28.9.27.0", {"start": v(28.08, -15.37) * mm, "end": v(26.11, -14.77) * mm});
            skLineSegment(sketch, "E28.2.28.0", {"start": v(30.73, -9) * mm, "end": v(28.9, -8.03) * mm});
            skLineSegment(sketch, "E28.3.28.0", {"start": v(30.43, -9.89) * mm, "end": v(30.73, -9) * mm});
            skLineSegment(sketch, "E28.6.28.0", {"start": v(30.43, -9.89) * mm, "end": v(30.14, -10.78) * mm});
            skLineSegment(sketch, "E28.9.28.0", {"start": v(30.14, -10.78) * mm, "end": v(28.1, -10.5) * mm});
            skLineSegment(sketch, "E28.2.29.0", {"start": v(31.75, -4.08) * mm, "end": v(29.8, -3.4) * mm});
            skLineSegment(sketch, "E28.3.29.0", {"start": v(31.6, -5) * mm, "end": v(31.75, -4.08) * mm});
            skLineSegment(sketch, "E28.6.29.0", {"start": v(31.6, -5) * mm, "end": v(31.46, -5.94) * mm});
            skLineSegment(sketch, "E28.9.29.0", {"start": v(31.46, -5.94) * mm, "end": v(29.4, -5.97) * mm});
            skLineSegment(sketch, "E28.2.30.0", {"start": v(32, 0.94) * mm, "end": v(29.97, 1.3) * mm});
            skLineSegment(sketch, "E28.3.30.0", {"start": v(32, 0) * mm, "end": v(32, 0.94) * mm});
            skLineSegment(sketch, "E28.6.30.0", {"start": v(32, 0) * mm, "end": v(32, -0.94) * mm});
            skLineSegment(sketch, "E28.9.30.0", {"start": v(32, -0.94) * mm, "end": v(29.97, -1.3) * mm});
            skLineSegment(sketch, "E28.2.31.0", {"start": v(31.46, 5.94) * mm, "end": v(29.4, 5.97) * mm});
            skLineSegment(sketch, "E28.3.31.0", {"start": v(31.6, 5) * mm, "end": v(31.46, 5.94) * mm});
            skLineSegment(sketch, "E28.6.31.0", {"start": v(31.6, 5) * mm, "end": v(31.75, 4.08) * mm});
            skLineSegment(sketch, "E28.9.31.0", {"start": v(31.75, 4.08) * mm, "end": v(29.8, 3.4) * mm});
            skLineSegment(sketch, "E28.2.32.0", {"start": v(30.14, 10.78) * mm, "end": v(28.1, 10.5) * mm});
            skLineSegment(sketch, "E28.3.32.0", {"start": v(30.43, 9.89) * mm, "end": v(30.14, 10.78) * mm});
            skLineSegment(sketch, "E28.6.32.0", {"start": v(30.43, 9.89) * mm, "end": v(30.73, 9) * mm});
            skLineSegment(sketch, "E28.9.32.0", {"start": v(30.73, 9) * mm, "end": v(28.9, 8.03) * mm});
            skLineSegment(sketch, "E28.2.33.0", {"start": v(28.08, 15.37) * mm, "end": v(26.11, 14.77) * mm});
            skLineSegment(sketch, "E28.3.33.0", {"start": v(28.51, 14.53) * mm, "end": v(28.08, 15.37) * mm});
            skLineSegment(sketch, "E28.6.33.0", {"start": v(28.51, 14.53) * mm, "end": v(28.94, 13.69) * mm});
            skLineSegment(sketch, "E28.9.33.0", {"start": v(28.94, 13.69) * mm, "end": v(27.3, 12.45) * mm});
            skLineSegment(sketch, "E28.2.34.0", {"start": v(25.33, 19.57) * mm, "end": v(23.48, 18.67) * mm});
            skLineSegment(sketch, "E28.3.34.0", {"start": v(25.89, 18.8) * mm, "end": v(25.33, 19.57) * mm});
            skLineSegment(sketch, "E28.6.34.0", {"start": v(25.89, 18.8) * mm, "end": v(26.44, 18.05) * mm});
            skLineSegment(sketch, "E28.9.34.0", {"start": v(26.44, 18.05) * mm, "end": v(25.01, 16.57) * mm});
            skLineSegment(sketch, "E28.2.35.0", {"start": v(21.96, 23.3) * mm, "end": v(20.27, 22.11) * mm});
            skLineSegment(sketch, "E28.3.35.0", {"start": v(22.63, 22.63) * mm, "end": v(21.96, 23.3) * mm});
            skLineSegment(sketch, "E28.6.35.0", {"start": v(22.63, 22.63) * mm, "end": v(23.3, 21.96) * mm});
            skLineSegment(sketch, "E28.9.35.0", {"start": v(23.3, 21.96) * mm, "end": v(22.11, 20.27) * mm});
            skLineSegment(sketch, "E28.2.36.0", {"start": v(18.05, 26.44) * mm, "end": v(16.57, 25.01) * mm});
            skLineSegment(sketch, "E28.3.36.0", {"start": v(18.8, 25.89) * mm, "end": v(18.05, 26.44) * mm});
            skLineSegment(sketch, "E28.6.36.0", {"start": v(18.8, 25.89) * mm, "end": v(19.57, 25.33) * mm});
            skLineSegment(sketch, "E28.9.36.0", {"start": v(19.57, 25.33) * mm, "end": v(18.67, 23.48) * mm});
            skLineSegment(sketch, "E28.2.37.0", {"start": v(13.69, 28.94) * mm, "end": v(12.45, 27.3) * mm});
            skLineSegment(sketch, "E28.3.37.0", {"start": v(14.53, 28.51) * mm, "end": v(13.69, 28.94) * mm});
            skLineSegment(sketch, "E28.6.37.0", {"start": v(14.53, 28.51) * mm, "end": v(15.37, 28.08) * mm});
            skLineSegment(sketch, "E28.9.37.0", {"start": v(15.37, 28.08) * mm, "end": v(14.77, 26.11) * mm});
            skLineSegment(sketch, "E28.2.38.0", {"start": v(9, 30.73) * mm, "end": v(8.03, 28.9) * mm});
            skLineSegment(sketch, "E28.3.38.0", {"start": v(9.89, 30.43) * mm, "end": v(9, 30.73) * mm});
            skLineSegment(sketch, "E28.6.38.0", {"start": v(9.89, 30.43) * mm, "end": v(10.78, 30.14) * mm});
            skLineSegment(sketch, "E28.9.38.0", {"start": v(10.78, 30.14) * mm, "end": v(10.5, 28.1) * mm});
            skLineSegment(sketch, "E28.2.39.0", {"start": v(4.08, 31.75) * mm, "end": v(3.4, 29.8) * mm});
            skLineSegment(sketch, "E28.3.39.0", {"start": v(5, 31.6) * mm, "end": v(4.08, 31.75) * mm});
            skLineSegment(sketch, "E28.6.39.0", {"start": v(5, 31.6) * mm, "end": v(5.94, 31.46) * mm});
            skLineSegment(sketch, "E28.9.39.0", {"start": v(5.94, 31.46) * mm, "end": v(5.97, 29.4) * mm});
            skSolve(sketch);
        }
        {
            var Q0;
            Q0 = qSketchRegion(id + "F14", true);
            extrude(context, id + "F15", {"entities" : qUnion([Q0]), "operationType" : NewBodyOperationType.ADD, "depth" : 4 * mm, "offsetDistance" : 25 * mm});
        }
        {
            var Q0;
            Q0=makeQuery(id+"F7.opExtrude","CAP_FACE",FACE,{"disambiguationData":[OSD([sQuery(id+"F0.wireOp",EDGE,"E0")])],"isStart":false});
            var sketch = newSketch(context, id + "F16", { "sketchPlane" : qUnion([Q0])});
            skCircle(sketch, "E29", {"center": v(40, 0) * mm, "radius": 7.5 * mm});
            skLineSegment(sketch, "E30", {"start": v(40, 0) * mm, "end": v(40, 7.5) * mm, "construction": true});
            skLineSegment(sketch, "E31", {"start": v(38.68, 7.38) * mm, "end": v(39.06, 9.5) * mm});
            skLineSegment(sketch, "E32", {"start": v(39.06, 9.5) * mm, "end": v(40.94, 9.5) * mm});
            skLineSegment(sketch, "E33.MirrorCS", {"start": v(41.32, 7.38) * mm, "end": v(40.94, 9.5) * mm});
            skLineSegment(sketch, "E34.1.0", {"start": v(33.65, 7.13) * mm, "end": v(35.18, 8.24) * mm});
            skLineSegment(sketch, "E34.1.1", {"start": v(36.72, 6.75) * mm, "end": v(35.18, 8.24) * mm});
            skLineSegment(sketch, "E34.1.2", {"start": v(34.6, 5.2) * mm, "end": v(33.65, 7.13) * mm});
            skLineSegment(sketch, "E34.2.0", {"start": v(30.67, 2.04) * mm, "end": v(31.26, 3.83) * mm});
            skLineSegment(sketch, "E34.2.1", {"start": v(33.38, 3.53) * mm, "end": v(31.26, 3.83) * mm});
            skLineSegment(sketch, "E34.2.2", {"start": v(32.57, 1.03) * mm, "end": v(30.67, 2.04) * mm});
            skLineSegment(sketch, "E35.1.3.0", {"start": v(31.26, -3.83) * mm, "end": v(30.67, -2.04) * mm});
            skLineSegment(sketch, "E35.3.3.0", {"start": v(32.57, -1.03) * mm, "end": v(30.67, -2.04) * mm});
            skLineSegment(sketch, "E35.6.3.0", {"start": v(33.38, -3.53) * mm, "end": v(31.26, -3.83) * mm});
            skLineSegment(sketch, "E35.1.4.0", {"start": v(35.18, -8.24) * mm, "end": v(33.65, -7.13) * mm});
            skLineSegment(sketch, "E35.3.4.0", {"start": v(34.6, -5.2) * mm, "end": v(33.65, -7.13) * mm});
            skLineSegment(sketch, "E35.6.4.0", {"start": v(36.72, -6.75) * mm, "end": v(35.18, -8.24) * mm});
            skLineSegment(sketch, "E35.1.5.0", {"start": v(40.94, -9.5) * mm, "end": v(39.06, -9.5) * mm});
            skLineSegment(sketch, "E35.3.5.0", {"start": v(38.68, -7.38) * mm, "end": v(39.06, -9.5) * mm});
            skLineSegment(sketch, "E35.6.5.0", {"start": v(41.32, -7.38) * mm, "end": v(40.94, -9.5) * mm});
            skLineSegment(sketch, "E35.1.6.0", {"start": v(46.35, -7.13) * mm, "end": v(44.82, -8.24) * mm});
            skLineSegment(sketch, "E35.3.6.0", {"start": v(43.28, -6.75) * mm, "end": v(44.82, -8.24) * mm});
            skLineSegment(sketch, "E35.6.6.0", {"start": v(45.4, -5.2) * mm, "end": v(46.35, -7.13) * mm});
            skLineSegment(sketch, "E35.1.7.0", {"start": v(49.33, -2.04) * mm, "end": v(48.74, -3.83) * mm});
            skLineSegment(sketch, "E35.3.7.0", {"start": v(46.62, -3.53) * mm, "end": v(48.74, -3.83) * mm});
            skLineSegment(sketch, "E35.6.7.0", {"start": v(47.43, -1.03) * mm, "end": v(49.33, -2.04) * mm});
            skLineSegment(sketch, "E35.1.8.0", {"start": v(48.74, 3.83) * mm, "end": v(49.33, 2.04) * mm});
            skLineSegment(sketch, "E35.3.8.0", {"start": v(47.43, 1.03) * mm, "end": v(49.33, 2.04) * mm});
            skLineSegment(sketch, "E35.6.8.0", {"start": v(46.62, 3.53) * mm, "end": v(48.74, 3.83) * mm});
            skLineSegment(sketch, "E35.1.9.0", {"start": v(44.82, 8.24) * mm, "end": v(46.35, 7.13) * mm});
            skLineSegment(sketch, "E35.3.9.0", {"start": v(45.4, 5.2) * mm, "end": v(46.35, 7.13) * mm});
            skLineSegment(sketch, "E35.6.9.0", {"start": v(43.28, 6.75) * mm, "end": v(44.82, 8.24) * mm});
            skSolve(sketch);
        }
        {
            var Q0;
            Q0 = qSketchRegion(id + "F16", true);
            extrude(context, id + "F17", {"entities" : qUnion([Q0]), "operationType" : NewBodyOperationType.ADD, "depth" : 4 * mm, "offsetDistance" : 25 * mm});
        }
        {
            var Q0;
            Q0=makeQuery(id+"F17.opExtrude","CAP_FACE",FACE,{"disambiguationData":[OSD([sQuery(id+"F16.wireOp",EDGE,"E29"),sQuery(id+"F16.wireOp",EDGE,"E31"),sQuery(id+"F16.wireOp",EDGE,"E32"),sQuery(id+"F16.wireOp",EDGE,"E33.MirrorCS"),sQuery(id+"F16.wireOp",EDGE,"E34.1.0"),sQuery(id+"F16.wireOp",EDGE,"E34.1.1"),sQuery(id+"F16.wireOp",EDGE,"E34.1.2"),sQuery(id+"F16.wireOp",EDGE,"E34.2.0"),sQuery(id+"F16.wireOp",EDGE,"E34.2.1"),sQuery(id+"F16.wireOp",EDGE,"E34.2.2"),sQuery(id+"F16.wireOp",EDGE,"E35.1.3.0"),sQuery(id+"F16.wireOp",EDGE,"E35.3.3.0"),sQuery(id+"F16.wireOp",EDGE,"E35.6.3.0"),sQuery(id+"F16.wireOp",EDGE,"E35.1.4.0"),sQuery(id+"F16.wireOp",EDGE,"E35.3.4.0"),sQuery(id+"F16.wireOp",EDGE,"E35.6.4.0"),sQuery(id+"F16.wireOp",EDGE,"E35.1.5.0"),sQuery(id+"F16.wireOp",EDGE,"E35.3.5.0"),sQuery(id+"F16.wireOp",EDGE,"E35.6.5.0"),sQuery(id+"F16.wireOp",EDGE,"E35.1.6.0"),sQuery(id+"F16.wireOp",EDGE,"E35.3.6.0"),sQuery(id+"F16.wireOp",EDGE,"E35.6.6.0"),sQuery(id+"F16.wireOp",EDGE,"E35.1.7.0"),sQuery(id+"F16.wireOp",EDGE,"E35.3.7.0"),sQuery(id+"F16.wireOp",EDGE,"E35.6.7.0"),sQuery(id+"F16.wireOp",EDGE,"E35.1.8.0"),sQuery(id+"F16.wireOp",EDGE,"E35.3.8.0"),sQuery(id+"F16.wireOp",EDGE,"E35.6.8.0"),sQuery(id+"F16.wireOp",EDGE,"E35.1.9.0"),sQuery(id+"F16.wireOp",EDGE,"E35.3.9.0"),sQuery(id+"F16.wireOp",EDGE,"E35.6.9.0")])],"isStart":false});
            var sketch = newSketch(context, id + "F18", { "sketchPlane" : qUnion([Q0])});
            skCircle(sketch, "E36.0", {"center": v(40, 0) * mm, "radius": 3 * mm});
            skSolve(sketch);
        }
        {
            var Q0;
            Q0 = qSketchRegion(id + "F18", true);
            extrude(context, id + "F19", {"entities" : qUnion([Q0]), "operationType" : NewBodyOperationType.ADD, "depth" : 2 * mm, "offsetDistance" : 25 * mm});
        }
        {
            var Q0;
            Q0=makeQuery(id+"F19.opExtrude","CAP_FACE",FACE,{"disambiguationData":[OSD([sQuery(id+"F18.wireOp",EDGE,"E36.0")])],"isStart":false});
            var sketch = newSketch(context, id + "F20", { "sketchPlane" : qUnion([Q0])});
            skCircle(sketch, "E37", {"center": v(0, 0) * mm, "radius": 98 * mm});
            skCircle(sketch, "E38.0", {"center": v(0, 0) * mm, "radius": 5.5 * mm});
            skSolve(sketch);
        }
        {
            var Q0;
            Q0 = qSketchRegion(id + "F20", true);
            extrude(context, id + "F21", {"entities" : qUnion([Q0]), "depth" : 1 * mm, "offsetDistance" : 25 * mm});
        }
        {
            var Q0;
            Q0=makeQuery(id+"F21.opExtrude","SWEPT_BODY",BODY,{"disambiguationData":[OSD([sQuery(id+"F20.wireOp",EDGE,"E37"),sQuery(id+"F20.wireOp",EDGE,"E38.0")])]});
            var Q1;
            Q1=makeQuery(id+"F1.opExtrude","SWEPT_BODY",BODY,{"disambiguationData":[OSD([sQuery(id+"F0.wireOp",EDGE,"E0")])]});
            booleanBodies(context, id + "F22", {"operationType" : BooleanOperationType.SUBTRACTION, "tools" : qUnion([Q0]), "targets" : qUnion([Q1]), "keepTools" : true});
        }
        {
            var Q0;
            Q0=makeQuery(id+"F21.opExtrude","CAP_FACE",FACE,{"disambiguationData":[OSD([sQuery(id+"F20.wireOp",EDGE,"E37"),sQuery(id+"F20.wireOp",EDGE,"E38.0")])],"isStart":true});
            var sketch = newSketch(context, id + "F23", { "sketchPlane" : qUnion([Q0])});
            skCircle(sketch, "E39.0", {"center": v(-40, 0) * mm, "radius": 3 * mm});
            skCircle(sketch, "E40", {"center": v(-40, 0) * mm, "radius": 5 * mm});
            skSolve(sketch);
        }
        {
            var Q0;
            Q0 = qSketchRegion(id + "F23", true);
            extrude(context, id + "F24", {"entities" : qUnion([Q0]), "operationType" : NewBodyOperationType.ADD, "endBound" : BoundingType.UP_TO_NEXT, "depth" : 25 * mm, "offsetDistance" : 25 * mm});
        }
        {
            var Q0;
            Q0=makeQuery(id+"F21.opExtrude","CAP_FACE",FACE,{"disambiguationData":[OSD([sQuery(id+"F20.wireOp",EDGE,"E37"),sQuery(id+"F20.wireOp",EDGE,"E38.0")])],"isStart":false});
            var sketch = newSketch(context, id + "F25", { "sketchPlane" : qUnion([Q0])});
            skLineSegment(sketch, "E41.bottom", {"start": v(1.5, 91) * mm, "end": v(-1.5, 91) * mm});
            skLineSegment(sketch, "E41.top", {"start": v(1.5, 71) * mm, "end": v(-1.5, 71) * mm});
            skLineSegment(sketch, "E41.left", {"start": v(1.5, 91) * mm, "end": v(1.5, 71) * mm});
            skLineSegment(sketch, "E41.right", {"start": v(-1.5, 91) * mm, "end": v(-1.5, 71) * mm});
            skPoint(sketch, "E41.middle", {"position": v(0, 81) * mm});
            skLineSegment(sketch, "E42.1.0", {"start": v(-44.2, 79.56) * mm, "end": v(-46.8, 78.06) * mm});
            skLineSegment(sketch, "E42.1.1", {"start": v(-44.2, 79.56) * mm, "end": v(-34.2, 62.24) * mm});
            skLineSegment(sketch, "E42.1.2", {"start": v(-46.8, 78.06) * mm, "end": v(-36.8, 60.74) * mm});
            skLineSegment(sketch, "E42.1.3", {"start": v(-34.2, 62.24) * mm, "end": v(-36.8, 60.74) * mm});
            skLineSegment(sketch, "E42.2.0", {"start": v(-78.06, 46.8) * mm, "end": v(-79.56, 44.2) * mm});
            skLineSegment(sketch, "E42.2.1", {"start": v(-78.06, 46.8) * mm, "end": v(-60.74, 36.8) * mm});
            skLineSegment(sketch, "E42.2.2", {"start": v(-79.56, 44.2) * mm, "end": v(-62.24, 34.2) * mm});
            skLineSegment(sketch, "E42.2.3", {"start": v(-60.74, 36.8) * mm, "end": v(-62.24, 34.2) * mm});
            skPoint(sketch, "E42.center", {"position": v(0, 0) * mm});
            skLineSegment(sketch, "E43.2.3.0", {"start": v(-91, 1.5) * mm, "end": v(-91, -1.5) * mm});
            skLineSegment(sketch, "E43.3.3.0", {"start": v(-91, 1.5) * mm, "end": v(-71, 1.5) * mm});
            skLineSegment(sketch, "E43.6.3.0", {"start": v(-91, -1.5) * mm, "end": v(-71, -1.5) * mm});
            skLineSegment(sketch, "E43.9.3.0", {"start": v(-71, 1.5) * mm, "end": v(-71, -1.5) * mm});
            skLineSegment(sketch, "E43.2.4.0", {"start": v(-79.56, -44.2) * mm, "end": v(-78.06, -46.8) * mm});
            skLineSegment(sketch, "E43.3.4.0", {"start": v(-79.56, -44.2) * mm, "end": v(-62.24, -34.2) * mm});
            skLineSegment(sketch, "E43.6.4.0", {"start": v(-78.06, -46.8) * mm, "end": v(-60.74, -36.8) * mm});
            skLineSegment(sketch, "E43.9.4.0", {"start": v(-62.24, -34.2) * mm, "end": v(-60.74, -36.8) * mm});
            skLineSegment(sketch, "E43.2.5.0", {"start": v(-46.8, -78.06) * mm, "end": v(-44.2, -79.56) * mm});
            skLineSegment(sketch, "E43.3.5.0", {"start": v(-46.8, -78.06) * mm, "end": v(-36.8, -60.74) * mm});
            skLineSegment(sketch, "E43.6.5.0", {"start": v(-44.2, -79.56) * mm, "end": v(-34.2, -62.24) * mm});
            skLineSegment(sketch, "E43.9.5.0", {"start": v(-36.8, -60.74) * mm, "end": v(-34.2, -62.24) * mm});
            skLineSegment(sketch, "E43.2.6.0", {"start": v(-1.5, -91) * mm, "end": v(1.5, -91) * mm});
            skLineSegment(sketch, "E43.3.6.0", {"start": v(-1.5, -91) * mm, "end": v(-1.5, -71) * mm});
            skLineSegment(sketch, "E43.6.6.0", {"start": v(1.5, -91) * mm, "end": v(1.5, -71) * mm});
            skLineSegment(sketch, "E43.9.6.0", {"start": v(-1.5, -71) * mm, "end": v(1.5, -71) * mm});
            skLineSegment(sketch, "E43.2.7.0", {"start": v(44.2, -79.56) * mm, "end": v(46.8, -78.06) * mm});
            skLineSegment(sketch, "E43.3.7.0", {"start": v(44.2, -79.56) * mm, "end": v(34.2, -62.24) * mm});
            skLineSegment(sketch, "E43.6.7.0", {"start": v(46.8, -78.06) * mm, "end": v(36.8, -60.74) * mm});
            skLineSegment(sketch, "E43.9.7.0", {"start": v(34.2, -62.24) * mm, "end": v(36.8, -60.74) * mm});
            skLineSegment(sketch, "E43.2.8.0", {"start": v(78.06, -46.8) * mm, "end": v(79.56, -44.2) * mm});
            skLineSegment(sketch, "E43.3.8.0", {"start": v(78.06, -46.8) * mm, "end": v(60.74, -36.8) * mm});
            skLineSegment(sketch, "E43.6.8.0", {"start": v(79.56, -44.2) * mm, "end": v(62.24, -34.2) * mm});
            skLineSegment(sketch, "E43.9.8.0", {"start": v(60.74, -36.8) * mm, "end": v(62.24, -34.2) * mm});
            skLineSegment(sketch, "E43.2.9.0", {"start": v(91, -1.5) * mm, "end": v(91, 1.5) * mm});
            skLineSegment(sketch, "E43.3.9.0", {"start": v(91, -1.5) * mm, "end": v(71, -1.5) * mm});
            skLineSegment(sketch, "E43.6.9.0", {"start": v(91, 1.5) * mm, "end": v(71, 1.5) * mm});
            skLineSegment(sketch, "E43.9.9.0", {"start": v(71, -1.5) * mm, "end": v(71, 1.5) * mm});
            skLineSegment(sketch, "E43.2.10.0", {"start": v(79.56, 44.2) * mm, "end": v(78.06, 46.8) * mm});
            skLineSegment(sketch, "E43.3.10.0", {"start": v(79.56, 44.2) * mm, "end": v(62.24, 34.2) * mm});
            skLineSegment(sketch, "E43.6.10.0", {"start": v(78.06, 46.8) * mm, "end": v(60.74, 36.8) * mm});
            skLineSegment(sketch, "E43.9.10.0", {"start": v(62.24, 34.2) * mm, "end": v(60.74, 36.8) * mm});
            skLineSegment(sketch, "E43.2.11.0", {"start": v(46.8, 78.06) * mm, "end": v(44.2, 79.56) * mm});
            skLineSegment(sketch, "E43.3.11.0", {"start": v(46.8, 78.06) * mm, "end": v(36.8, 60.74) * mm});
            skLineSegment(sketch, "E43.6.11.0", {"start": v(44.2, 79.56) * mm, "end": v(34.2, 62.24) * mm});
            skLineSegment(sketch, "E43.9.11.0", {"start": v(36.8, 60.74) * mm, "end": v(34.2, 62.24) * mm});
            skSolve(sketch);
        }
        {
            var Q0;
            Q0 = qSketchRegion(id + "F25", true);
            extrude(context, id + "F26", {"entities" : qUnion([Q0]), "operationType" : NewBodyOperationType.REMOVE, "oppositeDirection" : true, "depth" : 0.5 * mm, "offsetDistance" : 25 * mm});
        }
        {
            var Q0;
            Q0=makeQuery(id+"F21.opExtrude","CAP_FACE",FACE,{"disambiguationData":[OSD([sQuery(id+"F20.wireOp",EDGE,"E37"),sQuery(id+"F20.wireOp",EDGE,"E38.0")])],"isStart":false});
            var sketch = newSketch(context, id + "F27", { "sketchPlane" : qUnion([Q0])});
            skLineSegment(sketch, "E44.bottom", {"start": v(0.75, 90.5) * mm, "end": v(-0.75, 90.5) * mm});
            skLineSegment(sketch, "E44.top", {"start": v(0.75, 78.5) * mm, "end": v(-0.75, 78.5) * mm});
            skLineSegment(sketch, "E44.left", {"start": v(0.75, 90.5) * mm, "end": v(0.75, 78.5) * mm});
            skLineSegment(sketch, "E44.right", {"start": v(-0.75, 90.5) * mm, "end": v(-0.75, 78.5) * mm});
            skPoint(sketch, "E44.middle", {"position": v(0, 84.5) * mm});
            skLineSegment(sketch, "E45.1.0", {"start": v(-8.71, 90.08) * mm, "end": v(-10.2, 89.93) * mm});
            skLineSegment(sketch, "E45.1.1", {"start": v(-8.71, 90.08) * mm, "end": v(-7.46, 78.15) * mm});
            skLineSegment(sketch, "E45.1.2", {"start": v(-10.2, 89.93) * mm, "end": v(-8.95, 78) * mm});
            skLineSegment(sketch, "E45.1.3", {"start": v(-7.46, 78.15) * mm, "end": v(-8.95, 78) * mm});
            skLineSegment(sketch, "E45.2.0", {"start": v(-18.08, 88.68) * mm, "end": v(-19.55, 88.37) * mm});
            skLineSegment(sketch, "E45.2.1", {"start": v(-18.08, 88.68) * mm, "end": v(-15.59, 76.94) * mm});
            skLineSegment(sketch, "E45.2.2", {"start": v(-19.55, 88.37) * mm, "end": v(-17.05, 76.63) * mm});
            skLineSegment(sketch, "E45.2.3", {"start": v(-15.59, 76.94) * mm, "end": v(-17.05, 76.63) * mm});
            skPoint(sketch, "E45.center", {"position": v(0, 0) * mm});
            skLineSegment(sketch, "E46.2.3.0", {"start": v(-27.25, 86.3) * mm, "end": v(-28.68, 85.84) * mm});
            skLineSegment(sketch, "E46.3.3.0", {"start": v(-27.25, 86.3) * mm, "end": v(-23.54, 74.89) * mm});
            skLineSegment(sketch, "E46.6.3.0", {"start": v(-28.68, 85.84) * mm, "end": v(-24.97, 74.43) * mm});
            skLineSegment(sketch, "E46.9.3.0", {"start": v(-23.54, 74.89) * mm, "end": v(-24.97, 74.43) * mm});
            skLineSegment(sketch, "E46.2.4.0", {"start": v(-36.12, 82.98) * mm, "end": v(-37.5, 82.37) * mm});
            skLineSegment(sketch, "E46.3.4.0", {"start": v(-36.12, 82.98) * mm, "end": v(-31.24, 72.02) * mm});
            skLineSegment(sketch, "E46.6.4.0", {"start": v(-37.5, 82.37) * mm, "end": v(-32.61, 71.4) * mm});
            skLineSegment(sketch, "E46.9.4.0", {"start": v(-31.24, 72.02) * mm, "end": v(-32.61, 71.4) * mm});
            skLineSegment(sketch, "E46.2.5.0", {"start": v(-44.6, 78.75) * mm, "end": v(-45.9, 78) * mm});
            skLineSegment(sketch, "E46.3.5.0", {"start": v(-44.6, 78.75) * mm, "end": v(-38.6, 68.36) * mm});
            skLineSegment(sketch, "E46.6.5.0", {"start": v(-45.9, 78) * mm, "end": v(-39.9, 67.6) * mm});
            skLineSegment(sketch, "E46.9.5.0", {"start": v(-38.6, 68.36) * mm, "end": v(-39.9, 67.6) * mm});
            skLineSegment(sketch, "E46.2.6.0", {"start": v(-52.59, 73.66) * mm, "end": v(-53.8, 72.78) * mm});
            skLineSegment(sketch, "E46.3.6.0", {"start": v(-52.59, 73.66) * mm, "end": v(-45.53, 63.95) * mm});
            skLineSegment(sketch, "E46.6.6.0", {"start": v(-53.8, 72.78) * mm, "end": v(-46.75, 63.07) * mm});
            skLineSegment(sketch, "E46.9.6.0", {"start": v(-45.53, 63.95) * mm, "end": v(-46.75, 63.07) * mm});
            skLineSegment(sketch, "E46.2.7.0", {"start": v(-60, 67.76) * mm, "end": v(-61.11, 66.75) * mm});
            skLineSegment(sketch, "E46.3.7.0", {"start": v(-60, 67.76) * mm, "end": v(-51.97, 58.84) * mm});
            skLineSegment(sketch, "E46.6.7.0", {"start": v(-61.11, 66.75) * mm, "end": v(-53.08, 57.84) * mm});
            skLineSegment(sketch, "E46.9.7.0", {"start": v(-51.97, 58.84) * mm, "end": v(-53.08, 57.84) * mm});
            skLineSegment(sketch, "E46.2.8.0", {"start": v(-66.75, 61.11) * mm, "end": v(-67.76, 60) * mm});
            skLineSegment(sketch, "E46.3.8.0", {"start": v(-66.75, 61.11) * mm, "end": v(-57.84, 53.08) * mm});
            skLineSegment(sketch, "E46.6.8.0", {"start": v(-67.76, 60) * mm, "end": v(-58.84, 51.97) * mm});
            skLineSegment(sketch, "E46.9.8.0", {"start": v(-57.84, 53.08) * mm, "end": v(-58.84, 51.97) * mm});
            skLineSegment(sketch, "E46.2.9.0", {"start": v(-72.78, 53.8) * mm, "end": v(-73.66, 52.59) * mm});
            skLineSegment(sketch, "E46.3.9.0", {"start": v(-72.78, 53.8) * mm, "end": v(-63.07, 46.75) * mm});
            skLineSegment(sketch, "E46.6.9.0", {"start": v(-73.66, 52.59) * mm, "end": v(-63.95, 45.53) * mm});
            skLineSegment(sketch, "E46.9.9.0", {"start": v(-63.07, 46.75) * mm, "end": v(-63.95, 45.53) * mm});
            skLineSegment(sketch, "E46.2.10.0", {"start": v(-78, 45.9) * mm, "end": v(-78.75, 44.6) * mm});
            skLineSegment(sketch, "E46.3.10.0", {"start": v(-78, 45.9) * mm, "end": v(-67.6, 39.9) * mm});
            skLineSegment(sketch, "E46.6.10.0", {"start": v(-78.75, 44.6) * mm, "end": v(-68.36, 38.6) * mm});
            skLineSegment(sketch, "E46.9.10.0", {"start": v(-67.6, 39.9) * mm, "end": v(-68.36, 38.6) * mm});
            skLineSegment(sketch, "E46.2.11.0", {"start": v(-82.37, 37.5) * mm, "end": v(-82.98, 36.12) * mm});
            skLineSegment(sketch, "E46.3.11.0", {"start": v(-82.37, 37.5) * mm, "end": v(-71.4, 32.61) * mm});
            skLineSegment(sketch, "E46.6.11.0", {"start": v(-82.98, 36.12) * mm, "end": v(-72.02, 31.24) * mm});
            skLineSegment(sketch, "E46.9.11.0", {"start": v(-71.4, 32.61) * mm, "end": v(-72.02, 31.24) * mm});
            skLineSegment(sketch, "E46.2.12.0", {"start": v(-85.84, 28.68) * mm, "end": v(-86.3, 27.25) * mm});
            skLineSegment(sketch, "E46.3.12.0", {"start": v(-85.84, 28.68) * mm, "end": v(-74.43, 24.97) * mm});
            skLineSegment(sketch, "E46.6.12.0", {"start": v(-86.3, 27.25) * mm, "end": v(-74.89, 23.54) * mm});
            skLineSegment(sketch, "E46.9.12.0", {"start": v(-74.43, 24.97) * mm, "end": v(-74.89, 23.54) * mm});
            skLineSegment(sketch, "E46.2.13.0", {"start": v(-88.37, 19.55) * mm, "end": v(-88.68, 18.08) * mm});
            skLineSegment(sketch, "E46.3.13.0", {"start": v(-88.37, 19.55) * mm, "end": v(-76.63, 17.05) * mm});
            skLineSegment(sketch, "E46.6.13.0", {"start": v(-88.68, 18.08) * mm, "end": v(-76.94, 15.59) * mm});
            skLineSegment(sketch, "E46.9.13.0", {"start": v(-76.63, 17.05) * mm, "end": v(-76.94, 15.59) * mm});
            skLineSegment(sketch, "E46.2.14.0", {"start": v(-89.93, 10.2) * mm, "end": v(-90.08, 8.71) * mm});
            skLineSegment(sketch, "E46.3.14.0", {"start": v(-89.93, 10.2) * mm, "end": v(-78, 8.95) * mm});
            skLineSegment(sketch, "E46.6.14.0", {"start": v(-90.08, 8.71) * mm, "end": v(-78.15, 7.46) * mm});
            skLineSegment(sketch, "E46.9.14.0", {"start": v(-78, 8.95) * mm, "end": v(-78.15, 7.46) * mm});
            skLineSegment(sketch, "E46.2.15.0", {"start": v(-90.5, 0.75) * mm, "end": v(-90.5, -0.75) * mm});
            skLineSegment(sketch, "E46.3.15.0", {"start": v(-90.5, 0.75) * mm, "end": v(-78.5, 0.75) * mm});
            skLineSegment(sketch, "E46.6.15.0", {"start": v(-90.5, -0.75) * mm, "end": v(-78.5, -0.75) * mm});
            skLineSegment(sketch, "E46.9.15.0", {"start": v(-78.5, 0.75) * mm, "end": v(-78.5, -0.75) * mm});
            skLineSegment(sketch, "E46.2.16.0", {"start": v(-90.08, -8.71) * mm, "end": v(-89.93, -10.2) * mm});
            skLineSegment(sketch, "E46.3.16.0", {"start": v(-90.08, -8.71) * mm, "end": v(-78.15, -7.46) * mm});
            skLineSegment(sketch, "E46.6.16.0", {"start": v(-89.93, -10.2) * mm, "end": v(-78, -8.95) * mm});
            skLineSegment(sketch, "E46.9.16.0", {"start": v(-78.15, -7.46) * mm, "end": v(-78, -8.95) * mm});
            skLineSegment(sketch, "E46.2.17.0", {"start": v(-88.68, -18.08) * mm, "end": v(-88.37, -19.55) * mm});
            skLineSegment(sketch, "E46.3.17.0", {"start": v(-88.68, -18.08) * mm, "end": v(-76.94, -15.59) * mm});
            skLineSegment(sketch, "E46.6.17.0", {"start": v(-88.37, -19.55) * mm, "end": v(-76.63, -17.05) * mm});
            skLineSegment(sketch, "E46.9.17.0", {"start": v(-76.94, -15.59) * mm, "end": v(-76.63, -17.05) * mm});
            skLineSegment(sketch, "E46.2.18.0", {"start": v(-86.3, -27.25) * mm, "end": v(-85.84, -28.68) * mm});
            skLineSegment(sketch, "E46.3.18.0", {"start": v(-86.3, -27.25) * mm, "end": v(-74.89, -23.54) * mm});
            skLineSegment(sketch, "E46.6.18.0", {"start": v(-85.84, -28.68) * mm, "end": v(-74.43, -24.97) * mm});
            skLineSegment(sketch, "E46.9.18.0", {"start": v(-74.89, -23.54) * mm, "end": v(-74.43, -24.97) * mm});
            skLineSegment(sketch, "E46.2.19.0", {"start": v(-82.98, -36.12) * mm, "end": v(-82.37, -37.5) * mm});
            skLineSegment(sketch, "E46.3.19.0", {"start": v(-82.98, -36.12) * mm, "end": v(-72.02, -31.24) * mm});
            skLineSegment(sketch, "E46.6.19.0", {"start": v(-82.37, -37.5) * mm, "end": v(-71.4, -32.61) * mm});
            skLineSegment(sketch, "E46.9.19.0", {"start": v(-72.02, -31.24) * mm, "end": v(-71.4, -32.61) * mm});
            skLineSegment(sketch, "E46.2.20.0", {"start": v(-78.75, -44.6) * mm, "end": v(-78, -45.9) * mm});
            skLineSegment(sketch, "E46.3.20.0", {"start": v(-78.75, -44.6) * mm, "end": v(-68.36, -38.6) * mm});
            skLineSegment(sketch, "E46.6.20.0", {"start": v(-78, -45.9) * mm, "end": v(-67.6, -39.9) * mm});
            skLineSegment(sketch, "E46.9.20.0", {"start": v(-68.36, -38.6) * mm, "end": v(-67.6, -39.9) * mm});
            skLineSegment(sketch, "E46.2.21.0", {"start": v(-73.66, -52.59) * mm, "end": v(-72.78, -53.8) * mm});
            skLineSegment(sketch, "E46.3.21.0", {"start": v(-73.66, -52.59) * mm, "end": v(-63.95, -45.53) * mm});
            skLineSegment(sketch, "E46.6.21.0", {"start": v(-72.78, -53.8) * mm, "end": v(-63.07, -46.75) * mm});
            skLineSegment(sketch, "E46.9.21.0", {"start": v(-63.95, -45.53) * mm, "end": v(-63.07, -46.75) * mm});
            skLineSegment(sketch, "E46.2.22.0", {"start": v(-67.76, -60) * mm, "end": v(-66.75, -61.11) * mm});
            skLineSegment(sketch, "E46.3.22.0", {"start": v(-67.76, -60) * mm, "end": v(-58.84, -51.97) * mm});
            skLineSegment(sketch, "E46.6.22.0", {"start": v(-66.75, -61.11) * mm, "end": v(-57.84, -53.08) * mm});
            skLineSegment(sketch, "E46.9.22.0", {"start": v(-58.84, -51.97) * mm, "end": v(-57.84, -53.08) * mm});
            skLineSegment(sketch, "E46.2.23.0", {"start": v(-61.11, -66.75) * mm, "end": v(-60, -67.76) * mm});
            skLineSegment(sketch, "E46.3.23.0", {"start": v(-61.11, -66.75) * mm, "end": v(-53.08, -57.84) * mm});
            skLineSegment(sketch, "E46.6.23.0", {"start": v(-60, -67.76) * mm, "end": v(-51.97, -58.84) * mm});
            skLineSegment(sketch, "E46.9.23.0", {"start": v(-53.08, -57.84) * mm, "end": v(-51.97, -58.84) * mm});
            skLineSegment(sketch, "E46.2.24.0", {"start": v(-53.8, -72.78) * mm, "end": v(-52.59, -73.66) * mm});
            skLineSegment(sketch, "E46.3.24.0", {"start": v(-53.8, -72.78) * mm, "end": v(-46.75, -63.07) * mm});
            skLineSegment(sketch, "E46.6.24.0", {"start": v(-52.59, -73.66) * mm, "end": v(-45.53, -63.95) * mm});
            skLineSegment(sketch, "E46.9.24.0", {"start": v(-46.75, -63.07) * mm, "end": v(-45.53, -63.95) * mm});
            skLineSegment(sketch, "E46.2.25.0", {"start": v(-45.9, -78) * mm, "end": v(-44.6, -78.75) * mm});
            skLineSegment(sketch, "E46.3.25.0", {"start": v(-45.9, -78) * mm, "end": v(-39.9, -67.6) * mm});
            skLineSegment(sketch, "E46.6.25.0", {"start": v(-44.6, -78.75) * mm, "end": v(-38.6, -68.36) * mm});
            skLineSegment(sketch, "E46.9.25.0", {"start": v(-39.9, -67.6) * mm, "end": v(-38.6, -68.36) * mm});
            skLineSegment(sketch, "E46.2.26.0", {"start": v(-37.5, -82.37) * mm, "end": v(-36.12, -82.98) * mm});
            skLineSegment(sketch, "E46.3.26.0", {"start": v(-37.5, -82.37) * mm, "end": v(-32.61, -71.4) * mm});
            skLineSegment(sketch, "E46.6.26.0", {"start": v(-36.12, -82.98) * mm, "end": v(-31.24, -72.02) * mm});
            skLineSegment(sketch, "E46.9.26.0", {"start": v(-32.61, -71.4) * mm, "end": v(-31.24, -72.02) * mm});
            skLineSegment(sketch, "E46.2.27.0", {"start": v(-28.68, -85.84) * mm, "end": v(-27.25, -86.3) * mm});
            skLineSegment(sketch, "E46.3.27.0", {"start": v(-28.68, -85.84) * mm, "end": v(-24.97, -74.43) * mm});
            skLineSegment(sketch, "E46.6.27.0", {"start": v(-27.25, -86.3) * mm, "end": v(-23.54, -74.89) * mm});
            skLineSegment(sketch, "E46.9.27.0", {"start": v(-24.97, -74.43) * mm, "end": v(-23.54, -74.89) * mm});
            skLineSegment(sketch, "E46.2.28.0", {"start": v(-19.55, -88.37) * mm, "end": v(-18.08, -88.68) * mm});
            skLineSegment(sketch, "E46.3.28.0", {"start": v(-19.55, -88.37) * mm, "end": v(-17.05, -76.63) * mm});
            skLineSegment(sketch, "E46.6.28.0", {"start": v(-18.08, -88.68) * mm, "end": v(-15.59, -76.94) * mm});
            skLineSegment(sketch, "E46.9.28.0", {"start": v(-17.05, -76.63) * mm, "end": v(-15.59, -76.94) * mm});
            skLineSegment(sketch, "E46.2.29.0", {"start": v(-10.2, -89.93) * mm, "end": v(-8.71, -90.08) * mm});
            skLineSegment(sketch, "E46.3.29.0", {"start": v(-10.2, -89.93) * mm, "end": v(-8.95, -78) * mm});
            skLineSegment(sketch, "E46.6.29.0", {"start": v(-8.71, -90.08) * mm, "end": v(-7.46, -78.15) * mm});
            skLineSegment(sketch, "E46.9.29.0", {"start": v(-8.95, -78) * mm, "end": v(-7.46, -78.15) * mm});
            skLineSegment(sketch, "E46.2.30.0", {"start": v(-0.75, -90.5) * mm, "end": v(0.75, -90.5) * mm});
            skLineSegment(sketch, "E46.3.30.0", {"start": v(-0.75, -90.5) * mm, "end": v(-0.75, -78.5) * mm});
            skLineSegment(sketch, "E46.6.30.0", {"start": v(0.75, -90.5) * mm, "end": v(0.75, -78.5) * mm});
            skLineSegment(sketch, "E46.9.30.0", {"start": v(-0.75, -78.5) * mm, "end": v(0.75, -78.5) * mm});
            skLineSegment(sketch, "E46.2.31.0", {"start": v(8.71, -90.08) * mm, "end": v(10.2, -89.93) * mm});
            skLineSegment(sketch, "E46.3.31.0", {"start": v(8.71, -90.08) * mm, "end": v(7.46, -78.15) * mm});
            skLineSegment(sketch, "E46.6.31.0", {"start": v(10.2, -89.93) * mm, "end": v(8.95, -78) * mm});
            skLineSegment(sketch, "E46.9.31.0", {"start": v(7.46, -78.15) * mm, "end": v(8.95, -78) * mm});
            skLineSegment(sketch, "E46.2.32.0", {"start": v(18.08, -88.68) * mm, "end": v(19.55, -88.37) * mm});
            skLineSegment(sketch, "E46.3.32.0", {"start": v(18.08, -88.68) * mm, "end": v(15.59, -76.94) * mm});
            skLineSegment(sketch, "E46.6.32.0", {"start": v(19.55, -88.37) * mm, "end": v(17.05, -76.63) * mm});
            skLineSegment(sketch, "E46.9.32.0", {"start": v(15.59, -76.94) * mm, "end": v(17.05, -76.63) * mm});
            skLineSegment(sketch, "E46.2.33.0", {"start": v(27.25, -86.3) * mm, "end": v(28.68, -85.84) * mm});
            skLineSegment(sketch, "E46.3.33.0", {"start": v(27.25, -86.3) * mm, "end": v(23.54, -74.89) * mm});
            skLineSegment(sketch, "E46.6.33.0", {"start": v(28.68, -85.84) * mm, "end": v(24.97, -74.43) * mm});
            skLineSegment(sketch, "E46.9.33.0", {"start": v(23.54, -74.89) * mm, "end": v(24.97, -74.43) * mm});
            skLineSegment(sketch, "E46.2.34.0", {"start": v(36.12, -82.98) * mm, "end": v(37.5, -82.37) * mm});
            skLineSegment(sketch, "E46.3.34.0", {"start": v(36.12, -82.98) * mm, "end": v(31.24, -72.02) * mm});
            skLineSegment(sketch, "E46.6.34.0", {"start": v(37.5, -82.37) * mm, "end": v(32.61, -71.4) * mm});
            skLineSegment(sketch, "E46.9.34.0", {"start": v(31.24, -72.02) * mm, "end": v(32.61, -71.4) * mm});
            skLineSegment(sketch, "E46.2.35.0", {"start": v(44.6, -78.75) * mm, "end": v(45.9, -78) * mm});
            skLineSegment(sketch, "E46.3.35.0", {"start": v(44.6, -78.75) * mm, "end": v(38.6, -68.36) * mm});
            skLineSegment(sketch, "E46.6.35.0", {"start": v(45.9, -78) * mm, "end": v(39.9, -67.6) * mm});
            skLineSegment(sketch, "E46.9.35.0", {"start": v(38.6, -68.36) * mm, "end": v(39.9, -67.6) * mm});
            skLineSegment(sketch, "E46.2.36.0", {"start": v(52.59, -73.66) * mm, "end": v(53.8, -72.78) * mm});
            skLineSegment(sketch, "E46.3.36.0", {"start": v(52.59, -73.66) * mm, "end": v(45.53, -63.95) * mm});
            skLineSegment(sketch, "E46.6.36.0", {"start": v(53.8, -72.78) * mm, "end": v(46.75, -63.07) * mm});
            skLineSegment(sketch, "E46.9.36.0", {"start": v(45.53, -63.95) * mm, "end": v(46.75, -63.07) * mm});
            skLineSegment(sketch, "E46.2.37.0", {"start": v(60, -67.76) * mm, "end": v(61.11, -66.75) * mm});
            skLineSegment(sketch, "E46.3.37.0", {"start": v(60, -67.76) * mm, "end": v(51.97, -58.84) * mm});
            skLineSegment(sketch, "E46.6.37.0", {"start": v(61.11, -66.75) * mm, "end": v(53.08, -57.84) * mm});
            skLineSegment(sketch, "E46.9.37.0", {"start": v(51.97, -58.84) * mm, "end": v(53.08, -57.84) * mm});
            skLineSegment(sketch, "E46.2.38.0", {"start": v(66.75, -61.11) * mm, "end": v(67.76, -60) * mm});
            skLineSegment(sketch, "E46.3.38.0", {"start": v(66.75, -61.11) * mm, "end": v(57.84, -53.08) * mm});
            skLineSegment(sketch, "E46.6.38.0", {"start": v(67.76, -60) * mm, "end": v(58.84, -51.97) * mm});
            skLineSegment(sketch, "E46.9.38.0", {"start": v(57.84, -53.08) * mm, "end": v(58.84, -51.97) * mm});
            skLineSegment(sketch, "E46.2.39.0", {"start": v(72.78, -53.8) * mm, "end": v(73.66, -52.59) * mm});
            skLineSegment(sketch, "E46.3.39.0", {"start": v(72.78, -53.8) * mm, "end": v(63.07, -46.75) * mm});
            skLineSegment(sketch, "E46.6.39.0", {"start": v(73.66, -52.59) * mm, "end": v(63.95, -45.53) * mm});
            skLineSegment(sketch, "E46.9.39.0", {"start": v(63.07, -46.75) * mm, "end": v(63.95, -45.53) * mm});
            skLineSegment(sketch, "E46.2.40.0", {"start": v(78, -45.9) * mm, "end": v(78.75, -44.6) * mm});
            skLineSegment(sketch, "E46.3.40.0", {"start": v(78, -45.9) * mm, "end": v(67.6, -39.9) * mm});
            skLineSegment(sketch, "E46.6.40.0", {"start": v(78.75, -44.6) * mm, "end": v(68.36, -38.6) * mm});
            skLineSegment(sketch, "E46.9.40.0", {"start": v(67.6, -39.9) * mm, "end": v(68.36, -38.6) * mm});
            skLineSegment(sketch, "E46.2.41.0", {"start": v(82.37, -37.5) * mm, "end": v(82.98, -36.12) * mm});
            skLineSegment(sketch, "E46.3.41.0", {"start": v(82.37, -37.5) * mm, "end": v(71.4, -32.61) * mm});
            skLineSegment(sketch, "E46.6.41.0", {"start": v(82.98, -36.12) * mm, "end": v(72.02, -31.24) * mm});
            skLineSegment(sketch, "E46.9.41.0", {"start": v(71.4, -32.61) * mm, "end": v(72.02, -31.24) * mm});
            skLineSegment(sketch, "E46.2.42.0", {"start": v(85.84, -28.68) * mm, "end": v(86.3, -27.25) * mm});
            skLineSegment(sketch, "E46.3.42.0", {"start": v(85.84, -28.68) * mm, "end": v(74.43, -24.97) * mm});
            skLineSegment(sketch, "E46.6.42.0", {"start": v(86.3, -27.25) * mm, "end": v(74.89, -23.54) * mm});
            skLineSegment(sketch, "E46.9.42.0", {"start": v(74.43, -24.97) * mm, "end": v(74.89, -23.54) * mm});
            skLineSegment(sketch, "E46.2.43.0", {"start": v(88.37, -19.55) * mm, "end": v(88.68, -18.08) * mm});
            skLineSegment(sketch, "E46.3.43.0", {"start": v(88.37, -19.55) * mm, "end": v(76.63, -17.05) * mm});
            skLineSegment(sketch, "E46.6.43.0", {"start": v(88.68, -18.08) * mm, "end": v(76.94, -15.59) * mm});
            skLineSegment(sketch, "E46.9.43.0", {"start": v(76.63, -17.05) * mm, "end": v(76.94, -15.59) * mm});
            skLineSegment(sketch, "E46.2.44.0", {"start": v(89.93, -10.2) * mm, "end": v(90.08, -8.71) * mm});
            skLineSegment(sketch, "E46.3.44.0", {"start": v(89.93, -10.2) * mm, "end": v(78, -8.95) * mm});
            skLineSegment(sketch, "E46.6.44.0", {"start": v(90.08, -8.71) * mm, "end": v(78.15, -7.46) * mm});
            skLineSegment(sketch, "E46.9.44.0", {"start": v(78, -8.95) * mm, "end": v(78.15, -7.46) * mm});
            skLineSegment(sketch, "E46.2.45.0", {"start": v(90.5, -0.75) * mm, "end": v(90.5, 0.75) * mm});
            skLineSegment(sketch, "E46.3.45.0", {"start": v(90.5, -0.75) * mm, "end": v(78.5, -0.75) * mm});
            skLineSegment(sketch, "E46.6.45.0", {"start": v(90.5, 0.75) * mm, "end": v(78.5, 0.75) * mm});
            skLineSegment(sketch, "E46.9.45.0", {"start": v(78.5, -0.75) * mm, "end": v(78.5, 0.75) * mm});
            skLineSegment(sketch, "E46.2.46.0", {"start": v(90.08, 8.71) * mm, "end": v(89.93, 10.2) * mm});
            skLineSegment(sketch, "E46.3.46.0", {"start": v(90.08, 8.71) * mm, "end": v(78.15, 7.46) * mm});
            skLineSegment(sketch, "E46.6.46.0", {"start": v(89.93, 10.2) * mm, "end": v(78, 8.95) * mm});
            skLineSegment(sketch, "E46.9.46.0", {"start": v(78.15, 7.46) * mm, "end": v(78, 8.95) * mm});
            skLineSegment(sketch, "E46.2.47.0", {"start": v(88.68, 18.08) * mm, "end": v(88.37, 19.55) * mm});
            skLineSegment(sketch, "E46.3.47.0", {"start": v(88.68, 18.08) * mm, "end": v(76.94, 15.59) * mm});
            skLineSegment(sketch, "E46.6.47.0", {"start": v(88.37, 19.55) * mm, "end": v(76.63, 17.05) * mm});
            skLineSegment(sketch, "E46.9.47.0", {"start": v(76.94, 15.59) * mm, "end": v(76.63, 17.05) * mm});
            skLineSegment(sketch, "E46.2.48.0", {"start": v(86.3, 27.25) * mm, "end": v(85.84, 28.68) * mm});
            skLineSegment(sketch, "E46.3.48.0", {"start": v(86.3, 27.25) * mm, "end": v(74.89, 23.54) * mm});
            skLineSegment(sketch, "E46.6.48.0", {"start": v(85.84, 28.68) * mm, "end": v(74.43, 24.97) * mm});
            skLineSegment(sketch, "E46.9.48.0", {"start": v(74.89, 23.54) * mm, "end": v(74.43, 24.97) * mm});
            skLineSegment(sketch, "E46.2.49.0", {"start": v(82.98, 36.12) * mm, "end": v(82.37, 37.5) * mm});
            skLineSegment(sketch, "E46.3.49.0", {"start": v(82.98, 36.12) * mm, "end": v(72.02, 31.24) * mm});
            skLineSegment(sketch, "E46.6.49.0", {"start": v(82.37, 37.5) * mm, "end": v(71.4, 32.61) * mm});
            skLineSegment(sketch, "E46.9.49.0", {"start": v(72.02, 31.24) * mm, "end": v(71.4, 32.61) * mm});
            skLineSegment(sketch, "E46.2.50.0", {"start": v(78.75, 44.6) * mm, "end": v(78, 45.9) * mm});
            skLineSegment(sketch, "E46.3.50.0", {"start": v(78.75, 44.6) * mm, "end": v(68.36, 38.6) * mm});
            skLineSegment(sketch, "E46.6.50.0", {"start": v(78, 45.9) * mm, "end": v(67.6, 39.9) * mm});
            skLineSegment(sketch, "E46.9.50.0", {"start": v(68.36, 38.6) * mm, "end": v(67.6, 39.9) * mm});
            skLineSegment(sketch, "E46.2.51.0", {"start": v(73.66, 52.59) * mm, "end": v(72.78, 53.8) * mm});
            skLineSegment(sketch, "E46.3.51.0", {"start": v(73.66, 52.59) * mm, "end": v(63.95, 45.53) * mm});
            skLineSegment(sketch, "E46.6.51.0", {"start": v(72.78, 53.8) * mm, "end": v(63.07, 46.75) * mm});
            skLineSegment(sketch, "E46.9.51.0", {"start": v(63.95, 45.53) * mm, "end": v(63.07, 46.75) * mm});
            skLineSegment(sketch, "E46.2.52.0", {"start": v(67.76, 60) * mm, "end": v(66.75, 61.11) * mm});
            skLineSegment(sketch, "E46.3.52.0", {"start": v(67.76, 60) * mm, "end": v(58.84, 51.97) * mm});
            skLineSegment(sketch, "E46.6.52.0", {"start": v(66.75, 61.11) * mm, "end": v(57.84, 53.08) * mm});
            skLineSegment(sketch, "E46.9.52.0", {"start": v(58.84, 51.97) * mm, "end": v(57.84, 53.08) * mm});
            skLineSegment(sketch, "E46.2.53.0", {"start": v(61.11, 66.75) * mm, "end": v(60, 67.76) * mm});
            skLineSegment(sketch, "E46.3.53.0", {"start": v(61.11, 66.75) * mm, "end": v(53.08, 57.84) * mm});
            skLineSegment(sketch, "E46.6.53.0", {"start": v(60, 67.76) * mm, "end": v(51.97, 58.84) * mm});
            skLineSegment(sketch, "E46.9.53.0", {"start": v(53.08, 57.84) * mm, "end": v(51.97, 58.84) * mm});
            skLineSegment(sketch, "E46.2.54.0", {"start": v(53.8, 72.78) * mm, "end": v(52.59, 73.66) * mm});
            skLineSegment(sketch, "E46.3.54.0", {"start": v(53.8, 72.78) * mm, "end": v(46.75, 63.07) * mm});
            skLineSegment(sketch, "E46.6.54.0", {"start": v(52.59, 73.66) * mm, "end": v(45.53, 63.95) * mm});
            skLineSegment(sketch, "E46.9.54.0", {"start": v(46.75, 63.07) * mm, "end": v(45.53, 63.95) * mm});
            skLineSegment(sketch, "E46.2.55.0", {"start": v(45.9, 78) * mm, "end": v(44.6, 78.75) * mm});
            skLineSegment(sketch, "E46.3.55.0", {"start": v(45.9, 78) * mm, "end": v(39.9, 67.6) * mm});
            skLineSegment(sketch, "E46.6.55.0", {"start": v(44.6, 78.75) * mm, "end": v(38.6, 68.36) * mm});
            skLineSegment(sketch, "E46.9.55.0", {"start": v(39.9, 67.6) * mm, "end": v(38.6, 68.36) * mm});
            skLineSegment(sketch, "E46.2.56.0", {"start": v(37.5, 82.37) * mm, "end": v(36.12, 82.98) * mm});
            skLineSegment(sketch, "E46.3.56.0", {"start": v(37.5, 82.37) * mm, "end": v(32.61, 71.4) * mm});
            skLineSegment(sketch, "E46.6.56.0", {"start": v(36.12, 82.98) * mm, "end": v(31.24, 72.02) * mm});
            skLineSegment(sketch, "E46.9.56.0", {"start": v(32.61, 71.4) * mm, "end": v(31.24, 72.02) * mm});
            skLineSegment(sketch, "E46.2.57.0", {"start": v(28.68, 85.84) * mm, "end": v(27.25, 86.3) * mm});
            skLineSegment(sketch, "E46.3.57.0", {"start": v(28.68, 85.84) * mm, "end": v(24.97, 74.43) * mm});
            skLineSegment(sketch, "E46.6.57.0", {"start": v(27.25, 86.3) * mm, "end": v(23.54, 74.89) * mm});
            skLineSegment(sketch, "E46.9.57.0", {"start": v(24.97, 74.43) * mm, "end": v(23.54, 74.89) * mm});
            skLineSegment(sketch, "E46.2.58.0", {"start": v(19.55, 88.37) * mm, "end": v(18.08, 88.68) * mm});
            skLineSegment(sketch, "E46.3.58.0", {"start": v(19.55, 88.37) * mm, "end": v(17.05, 76.63) * mm});
            skLineSegment(sketch, "E46.6.58.0", {"start": v(18.08, 88.68) * mm, "end": v(15.59, 76.94) * mm});
            skLineSegment(sketch, "E46.9.58.0", {"start": v(17.05, 76.63) * mm, "end": v(15.59, 76.94) * mm});
            skLineSegment(sketch, "E46.2.59.0", {"start": v(10.2, 89.93) * mm, "end": v(8.71, 90.08) * mm});
            skLineSegment(sketch, "E46.3.59.0", {"start": v(10.2, 89.93) * mm, "end": v(8.95, 78) * mm});
            skLineSegment(sketch, "E46.6.59.0", {"start": v(8.71, 90.08) * mm, "end": v(7.46, 78.15) * mm});
            skLineSegment(sketch, "E46.9.59.0", {"start": v(8.95, 78) * mm, "end": v(7.46, 78.15) * mm});
            skSolve(sketch);
        }
        {
            var Q0;
            Q0 = qSketchRegion(id + "F27", true);
            extrude(context, id + "F28", {"entities" : qUnion([Q0]), "operationType" : NewBodyOperationType.REMOVE, "oppositeDirection" : true, "depth" : 0.2 * mm, "offsetDistance" : 25 * mm});
        }
        {
            var Q0;
            Q0=makeQuery(id+"F26.boolean.opBoolean","COPY",FACE,{"derivedFrom":makeQuery(id+"F26.opExtrude","CAP_FACE",FACE,{"disambiguationData":[OSD([sQuery(id+"F25.wireOp",EDGE,"E41.bottom"),sQuery(id+"F25.wireOp",EDGE,"E41.top"),sQuery(id+"F25.wireOp",EDGE,"E41.left"),sQuery(id+"F25.wireOp",EDGE,"E41.right")])],"isStart":false})});
            extrude(context, id + "F29", {"entities" : qUnion([Q0]), "depth" : 1 * mm, "offsetDistance" : 25 * mm});
        }
        {
            var Q0;
            Q0=makeQuery(id+"F28.boolean.opBoolean","COPY",FACE,{"derivedFrom":makeQuery(id+"F28.opExtrude","CAP_FACE",FACE,{"disambiguationData":[OSD([sQuery(id+"F27.wireOp",EDGE,"E46.2.59.0"),sQuery(id+"F27.wireOp",EDGE,"E46.3.59.0"),sQuery(id+"F27.wireOp",EDGE,"E46.6.59.0"),sQuery(id+"F27.wireOp",EDGE,"E46.9.59.0")])],"isStart":false})});
            extrude(context, id + "F30", {"entities" : qUnion([Q0]), "depth" : 0.4 * mm, "offsetDistance" : 25 * mm});
        }
        {
            var Q0;
            Q0=makeQuery(id+"F15.opExtrude","CAP_FACE",FACE,{"disambiguationData":[OSD([sQuery(id+"F14.wireOp",EDGE,"E21.0"),sQuery(id+"F14.wireOp",EDGE,"E22"),sQuery(id+"F14.wireOp",EDGE,"E23"),sQuery(id+"F14.wireOp",EDGE,"E24"),sQuery(id+"F14.wireOp",EDGE,"E25.MirrorCS"),sQuery(id+"F14.wireOp",EDGE,"E26.MirrorCS"),sQuery(id+"F14.wireOp",EDGE,"E27.1.0"),sQuery(id+"F14.wireOp",EDGE,"E27.1.1"),sQuery(id+"F14.wireOp",EDGE,"E27.1.2"),sQuery(id+"F14.wireOp",EDGE,"E27.1.3"),sQuery(id+"F14.wireOp",EDGE,"E27.2.0"),sQuery(id+"F14.wireOp",EDGE,"E27.2.1"),sQuery(id+"F14.wireOp",EDGE,"E27.2.2"),sQuery(id+"F14.wireOp",EDGE,"E27.2.3"),sQuery(id+"F14.wireOp",EDGE,"E28.2.3.0"),sQuery(id+"F14.wireOp",EDGE,"E28.3.3.0"),sQuery(id+"F14.wireOp",EDGE,"E28.6.3.0"),sQuery(id+"F14.wireOp",EDGE,"E28.9.3.0"),sQuery(id+"F14.wireOp",EDGE,"E28.2.4.0"),sQuery(id+"F14.wireOp",EDGE,"E28.3.4.0"),sQuery(id+"F14.wireOp",EDGE,"E28.6.4.0"),sQuery(id+"F14.wireOp",EDGE,"E28.9.4.0"),sQuery(id+"F14.wireOp",EDGE,"E28.2.5.0"),sQuery(id+"F14.wireOp",EDGE,"E28.3.5.0"),sQuery(id+"F14.wireOp",EDGE,"E28.6.5.0"),sQuery(id+"F14.wireOp",EDGE,"E28.9.5.0"),sQuery(id+"F14.wireOp",EDGE,"E28.2.6.0"),sQuery(id+"F14.wireOp",EDGE,"E28.3.6.0"),sQuery(id+"F14.wireOp",EDGE,"E28.6.6.0"),sQuery(id+"F14.wireOp",EDGE,"E28.9.6.0"),sQuery(id+"F14.wireOp",EDGE,"E28.2.7.0"),sQuery(id+"F14.wireOp",EDGE,"E28.3.7.0"),sQuery(id+"F14.wireOp",EDGE,"E28.6.7.0"),sQuery(id+"F14.wireOp",EDGE,"E28.9.7.0"),sQuery(id+"F14.wireOp",EDGE,"E28.2.8.0"),sQuery(id+"F14.wireOp",EDGE,"E28.3.8.0"),sQuery(id+"F14.wireOp",EDGE,"E28.6.8.0"),sQuery(id+"F14.wireOp",EDGE,"E28.9.8.0"),sQuery(id+"F14.wireOp",EDGE,"E28.2.9.0"),sQuery(id+"F14.wireOp",EDGE,"E28.3.9.0"),sQuery(id+"F14.wireOp",EDGE,"E28.6.9.0"),sQuery(id+"F14.wireOp",EDGE,"E28.9.9.0"),sQuery(id+"F14.wireOp",EDGE,"E28.2.10.0"),sQuery(id+"F14.wireOp",EDGE,"E28.3.10.0"),sQuery(id+"F14.wireOp",EDGE,"E28.6.10.0"),sQuery(id+"F14.wireOp",EDGE,"E28.9.10.0"),sQuery(id+"F14.wireOp",EDGE,"E28.2.11.0"),sQuery(id+"F14.wireOp",EDGE,"E28.3.11.0"),sQuery(id+"F14.wireOp",EDGE,"E28.6.11.0"),sQuery(id+"F14.wireOp",EDGE,"E28.9.11.0"),sQuery(id+"F14.wireOp",EDGE,"E28.2.12.0"),sQuery(id+"F14.wireOp",EDGE,"E28.3.12.0"),sQuery(id+"F14.wireOp",EDGE,"E28.6.12.0"),sQuery(id+"F14.wireOp",EDGE,"E28.9.12.0"),sQuery(id+"F14.wireOp",EDGE,"E28.2.13.0"),sQuery(id+"F14.wireOp",EDGE,"E28.3.13.0"),sQuery(id+"F14.wireOp",EDGE,"E28.6.13.0"),sQuery(id+"F14.wireOp",EDGE,"E28.9.13.0"),sQuery(id+"F14.wireOp",EDGE,"E28.2.14.0"),sQuery(id+"F14.wireOp",EDGE,"E28.3.14.0"),sQuery(id+"F14.wireOp",EDGE,"E28.6.14.0"),sQuery(id+"F14.wireOp",EDGE,"E28.9.14.0"),sQuery(id+"F14.wireOp",EDGE,"E28.2.15.0"),sQuery(id+"F14.wireOp",EDGE,"E28.3.15.0"),sQuery(id+"F14.wireOp",EDGE,"E28.6.15.0"),sQuery(id+"F14.wireOp",EDGE,"E28.9.15.0"),sQuery(id+"F14.wireOp",EDGE,"E28.2.16.0"),sQuery(id+"F14.wireOp",EDGE,"E28.3.16.0"),sQuery(id+"F14.wireOp",EDGE,"E28.6.16.0"),sQuery(id+"F14.wireOp",EDGE,"E28.9.16.0"),sQuery(id+"F14.wireOp",EDGE,"E28.2.17.0"),sQuery(id+"F14.wireOp",EDGE,"E28.3.17.0"),sQuery(id+"F14.wireOp",EDGE,"E28.6.17.0"),sQuery(id+"F14.wireOp",EDGE,"E28.9.17.0"),sQuery(id+"F14.wireOp",EDGE,"E28.2.18.0"),sQuery(id+"F14.wireOp",EDGE,"E28.3.18.0"),sQuery(id+"F14.wireOp",EDGE,"E28.6.18.0"),sQuery(id+"F14.wireOp",EDGE,"E28.9.18.0"),sQuery(id+"F14.wireOp",EDGE,"E28.2.19.0"),sQuery(id+"F14.wireOp",EDGE,"E28.3.19.0"),sQuery(id+"F14.wireOp",EDGE,"E28.6.19.0"),sQuery(id+"F14.wireOp",EDGE,"E28.9.19.0"),sQuery(id+"F14.wireOp",EDGE,"E28.2.20.0"),sQuery(id+"F14.wireOp",EDGE,"E28.3.20.0"),sQuery(id+"F14.wireOp",EDGE,"E28.6.20.0"),sQuery(id+"F14.wireOp",EDGE,"E28.9.20.0"),sQuery(id+"F14.wireOp",EDGE,"E28.2.21.0"),sQuery(id+"F14.wireOp",EDGE,"E28.3.21.0"),sQuery(id+"F14.wireOp",EDGE,"E28.6.21.0"),sQuery(id+"F14.wireOp",EDGE,"E28.9.21.0"),sQuery(id+"F14.wireOp",EDGE,"E28.2.22.0"),sQuery(id+"F14.wireOp",EDGE,"E28.3.22.0"),sQuery(id+"F14.wireOp",EDGE,"E28.6.22.0"),sQuery(id+"F14.wireOp",EDGE,"E28.9.22.0"),sQuery(id+"F14.wireOp",EDGE,"E28.2.23.0"),sQuery(id+"F14.wireOp",EDGE,"E28.3.23.0"),sQuery(id+"F14.wireOp",EDGE,"E28.6.23.0"),sQuery(id+"F14.wireOp",EDGE,"E28.9.23.0"),sQuery(id+"F14.wireOp",EDGE,"E28.2.24.0"),sQuery(id+"F14.wireOp",EDGE,"E28.3.24.0"),sQuery(id+"F14.wireOp",EDGE,"E28.6.24.0"),sQuery(id+"F14.wireOp",EDGE,"E28.9.24.0"),sQuery(id+"F14.wireOp",EDGE,"E28.2.25.0"),sQuery(id+"F14.wireOp",EDGE,"E28.3.25.0"),sQuery(id+"F14.wireOp",EDGE,"E28.6.25.0"),sQuery(id+"F14.wireOp",EDGE,"E28.9.25.0"),sQuery(id+"F14.wireOp",EDGE,"E28.2.26.0"),sQuery(id+"F14.wireOp",EDGE,"E28.3.26.0"),sQuery(id+"F14.wireOp",EDGE,"E28.6.26.0"),sQuery(id+"F14.wireOp",EDGE,"E28.9.26.0"),sQuery(id+"F14.wireOp",EDGE,"E28.2.27.0"),sQuery(id+"F14.wireOp",EDGE,"E28.3.27.0"),sQuery(id+"F14.wireOp",EDGE,"E28.6.27.0"),sQuery(id+"F14.wireOp",EDGE,"E28.9.27.0"),sQuery(id+"F14.wireOp",EDGE,"E28.2.28.0"),sQuery(id+"F14.wireOp",EDGE,"E28.3.28.0"),sQuery(id+"F14.wireOp",EDGE,"E28.6.28.0"),sQuery(id+"F14.wireOp",EDGE,"E28.9.28.0"),sQuery(id+"F14.wireOp",EDGE,"E28.2.29.0"),sQuery(id+"F14.wireOp",EDGE,"E28.3.29.0"),sQuery(id+"F14.wireOp",EDGE,"E28.6.29.0"),sQuery(id+"F14.wireOp",EDGE,"E28.9.29.0"),sQuery(id+"F14.wireOp",EDGE,"E28.2.30.0"),sQuery(id+"F14.wireOp",EDGE,"E28.3.30.0"),sQuery(id+"F14.wireOp",EDGE,"E28.6.30.0"),sQuery(id+"F14.wireOp",EDGE,"E28.9.30.0"),sQuery(id+"F14.wireOp",EDGE,"E28.2.31.0"),sQuery(id+"F14.wireOp",EDGE,"E28.3.31.0"),sQuery(id+"F14.wireOp",EDGE,"E28.6.31.0"),sQuery(id+"F14.wireOp",EDGE,"E28.9.31.0"),sQuery(id+"F14.wireOp",EDGE,"E28.2.32.0"),sQuery(id+"F14.wireOp",EDGE,"E28.3.32.0"),sQuery(id+"F14.wireOp",EDGE,"E28.6.32.0"),sQuery(id+"F14.wireOp",EDGE,"E28.9.32.0"),sQuery(id+"F14.wireOp",EDGE,"E28.2.33.0"),sQuery(id+"F14.wireOp",EDGE,"E28.3.33.0"),sQuery(id+"F14.wireOp",EDGE,"E28.6.33.0"),sQuery(id+"F14.wireOp",EDGE,"E28.9.33.0"),sQuery(id+"F14.wireOp",EDGE,"E28.2.34.0"),sQuery(id+"F14.wireOp",EDGE,"E28.3.34.0"),sQuery(id+"F14.wireOp",EDGE,"E28.6.34.0"),sQuery(id+"F14.wireOp",EDGE,"E28.9.34.0"),sQuery(id+"F14.wireOp",EDGE,"E28.2.35.0"),sQuery(id+"F14.wireOp",EDGE,"E28.3.35.0"),sQuery(id+"F14.wireOp",EDGE,"E28.6.35.0"),sQuery(id+"F14.wireOp",EDGE,"E28.9.35.0"),sQuery(id+"F14.wireOp",EDGE,"E28.2.36.0"),sQuery(id+"F14.wireOp",EDGE,"E28.3.36.0"),sQuery(id+"F14.wireOp",EDGE,"E28.6.36.0"),sQuery(id+"F14.wireOp",EDGE,"E28.9.36.0"),sQuery(id+"F14.wireOp",EDGE,"E28.2.37.0"),sQuery(id+"F14.wireOp",EDGE,"E28.3.37.0"),sQuery(id+"F14.wireOp",EDGE,"E28.6.37.0"),sQuery(id+"F14.wireOp",EDGE,"E28.9.37.0"),sQuery(id+"F14.wireOp",EDGE,"E28.2.38.0"),sQuery(id+"F14.wireOp",EDGE,"E28.3.38.0"),sQuery(id+"F14.wireOp",EDGE,"E28.6.38.0"),sQuery(id+"F14.wireOp",EDGE,"E28.9.38.0"),sQuery(id+"F14.wireOp",EDGE,"E28.2.39.0"),sQuery(id+"F14.wireOp",EDGE,"E28.3.39.0"),sQuery(id+"F14.wireOp",EDGE,"E28.6.39.0"),sQuery(id+"F14.wireOp",EDGE,"E28.9.39.0")])],"isStart":false});
            var sketch = newSketch(context, id + "F31", { "sketchPlane" : qUnion([Q0])});
            skCircle(sketch, "E47.0", {"center": v(0, 0) * mm, "radius": 3 * mm});
            skCircle(sketch, "E48.0", {"center": v(0, 0) * mm, "radius": 5.5 * mm});
            skSolve(sketch);
        }
        {
            var Q0;
            Q0 = qSketchRegion(id + "F31", true);
            extrude(context, id + "F32", {"entities" : qUnion([Q0]), "operationType" : NewBodyOperationType.ADD, "depth" : 5 * mm, "offsetDistance" : 25 * mm});
        }
        {
            var Q0;
            Q0=makeQuery(id+"F32.opExtrude","CAP_FACE",FACE,{"disambiguationData":[OSD([sQuery(id+"F31.wireOp",EDGE,"E47.0"),sQuery(id+"F31.wireOp",EDGE,"E48.0")])],"isStart":false});
            var sketch = newSketch(context, id + "F33", { "sketchPlane" : qUnion([Q0])});
            skCircle(sketch, "E49.0", {"center": v(0, 0) * mm, "radius": 3 * mm});
            skLineSegment(sketch, "E50", {"start": v(0, 50) * mm, "end": v(1.5, 50) * mm});
            skLineSegment(sketch, "E51", {"start": v(1.5, 50) * mm, "end": v(3, 4.6) * mm});
            skLineSegment(sketch, "E52.MirrorCS", {"start": v(0, 50) * mm, "end": v(-1.5, 50) * mm});
            skLineSegment(sketch, "E53.MirrorCS", {"start": v(-1.5, 50) * mm, "end": v(-3, 4.6) * mm});
            skCircle(sketch, "E54.0", {"center": v(0, 0) * mm, "radius": 5.5 * mm});
            skSolve(sketch);
        }
        {
            var Q0;
            Q0 = qSketchRegion(id + "F33", true);
            extrude(context, id + "F34", {"entities" : qUnion([Q0]), "operationType" : NewBodyOperationType.ADD, "depth" : 1 * mm, "offsetDistance" : 25 * mm});
        }
        {
            var Q0;
            Q0=makeQuery(id+"F6.opExtrude","CAP_FACE",FACE,{"disambiguationData":[OSD([sQuery(id+"F0.wireOp",EDGE,"E0")])],"isStart":false});
            var sketch = newSketch(context, id + "F35", { "sketchPlane" : qUnion([Q0])});
            skCircle(sketch, "E55", {"center": v(0, 0) * mm, "radius": 5.5 * mm});
            skLineSegment(sketch, "E56", {"start": v(0, 80) * mm, "end": v(0.5, 80) * mm});
            skLineSegment(sketch, "E57", {"start": v(0.5, 80) * mm, "end": v(2, 5.12) * mm});
            skLineSegment(sketch, "E58.MirrorCS", {"start": v(0, 80) * mm, "end": v(-0.5, 80) * mm});
            skLineSegment(sketch, "E59.MirrorCS", {"start": v(-0.5, 80) * mm, "end": v(-2, 5.12) * mm});
            skSolve(sketch);
        }
        {
            var Q0;
            Q0 = qSketchRegion(id + "F35", true);
            extrude(context, id + "F36", {"entities" : qUnion([Q0]), "operationType" : NewBodyOperationType.ADD, "oppositeDirection" : true, "depth" : 1 * mm, "offsetDistance" : 25 * mm});
        }
    });
